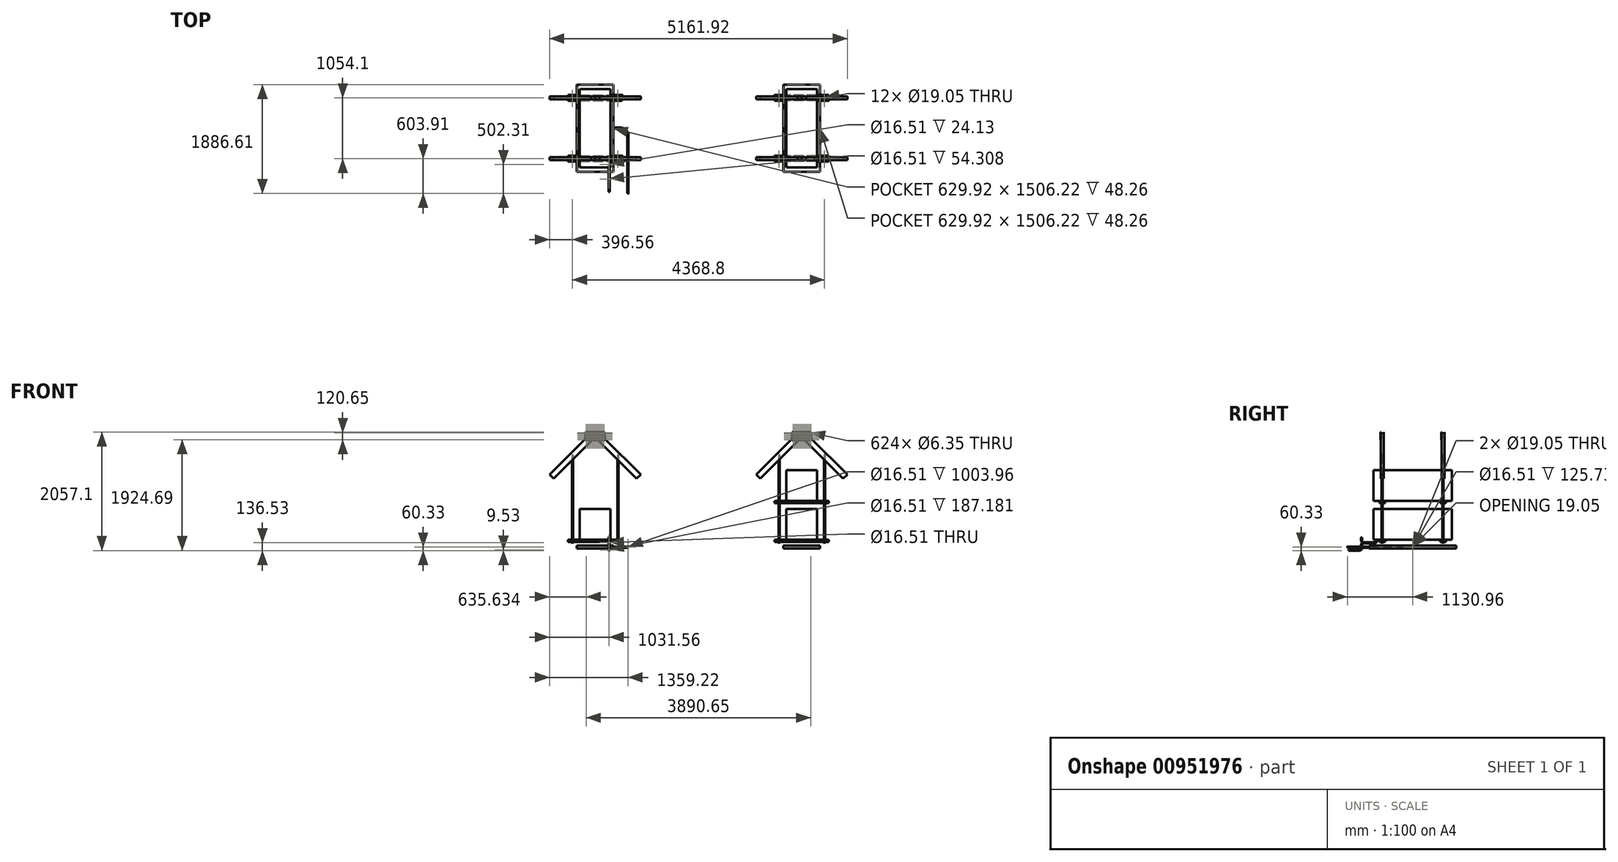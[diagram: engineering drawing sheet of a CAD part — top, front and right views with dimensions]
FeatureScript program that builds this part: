
annotation { "Feature Type Name" : "Feature", "Feature Type Description" : "" }
export const myFeature = defineFeature(function(context is Context, id is Id, definition is map)
    precondition{}
    {
        {
            var Q0;
            Q0=qCreatedBy(makeId("Front.planeOp"),FACE);
            var sketch = newSketch(context, id + "F0", { "sketchPlane" : qUnion([Q0])});
            skLineSegment(sketch, "E0.bottom", {"start": v(-266.7, 266.7) * mm, "end": v(266.7, 266.7) * mm});
            skLineSegment(sketch, "E0.top", {"start": v(-266.7, -266.7) * mm, "end": v(266.7, -266.7) * mm});
            skLineSegment(sketch, "E0.left", {"start": v(-266.7, 266.7) * mm, "end": v(-266.7, -266.7) * mm});
            skLineSegment(sketch, "E0.right", {"start": v(266.7, 266.7) * mm, "end": v(266.7, -266.7) * mm});
            skSolve(sketch);
        }
        {
            var Q0;
            Q0=qSketchRegion(id+"F0",true);
            extrude(context, id + "F1", {"entities" : qUnion([Q0]), "endBound" : BoundingType.SYMMETRIC, "depth" : 1358.9 * mm, "offsetDistance" : 25.4 * mm});
        }
        {
            var Q0;
            Q0=makeQuery(id+"F1.opExtrude","SWEPT_FACE",FACE,{"disambiguationData":[OSD([sQuery(id+"F0.wireOp",EDGE,"E0.top")])]});
            var sketch = newSketch(context, id + "F2", { "sketchPlane" : qUnion([Q0])});
            skLineSegment(sketch, "E1.bottom", {"start": v(-469.9, 577.85) * mm, "end": v(469.9, 577.85) * mm});
            skLineSegment(sketch, "E1.top", {"start": v(-469.9, 476.25) * mm, "end": v(469.9, 476.25) * mm});
            skLineSegment(sketch, "E1.left", {"start": v(-469.9, 577.85) * mm, "end": v(-469.9, 476.25) * mm});
            skLineSegment(sketch, "E1.right", {"start": v(469.9, 577.85) * mm, "end": v(469.9, 476.25) * mm});
            skLineSegment(sketch, "E2.bottom", {"start": v(-469.9, -476.25) * mm, "end": v(469.9, -476.25) * mm});
            skLineSegment(sketch, "E2.top", {"start": v(-469.9, -577.85) * mm, "end": v(469.9, -577.85) * mm});
            skLineSegment(sketch, "E2.left", {"start": v(-469.9, -476.25) * mm, "end": v(-469.9, -577.85) * mm});
            skLineSegment(sketch, "E2.right", {"start": v(469.9, -476.25) * mm, "end": v(469.9, -577.85) * mm});
            skSolve(sketch);
        }
        {
            var Q0;
            Q0=qSketchRegion(id+"F2",true);
            extrude(context, id + "F3", {"entities" : qUnion([Q0]), "operationType" : NewBodyOperationType.ADD, "depth" : 38.1 * mm, "offsetDistance" : 25.4 * mm});
        }
        {
            var Q0;
            {var subQ0=sQuery(id+"F2.wireOp",EDGE,"E1.top");var subQ1=sQuery(id+"F2.wireOp",EDGE,"E1.bottom");var subQ2=sQuery(id+"F2.wireOp",EDGE,"E1.right");Q0=makeQuery(id+"F3.boolean.opBoolean","SPLIT",FACE,{"disambiguationData":[TD([makeQuery(id+"F1.opExtrude","SWEPT_FACE",FACE,{"disambiguationData":[OSD([sQuery(id+"F0.wireOp",EDGE,"E0.right")])]})])],"derivedFrom":makeQuery(id+"F3.opExtrude","CAP_FACE",FACE,{"disambiguationData":[OSD([subQ1,subQ0,sQuery(id+"F2.wireOp",EDGE,"E1.left"),subQ2])],"isStart":true})});}
            var sketch = newSketch(context, id + "F4", { "sketchPlane" : qUnion([Q0])});
            skPoint(sketch, "E3", {"position": v(393.7, -527.05) * mm});
            skPoint(sketch, "E4", {"position": v(-393.7, -527.05) * mm});
            skSolve(sketch);
        }
        {
            var Q0;
            {var subQ0=sQuery(id+"F2.wireOp",EDGE,"E2.top");var subQ1=sQuery(id+"F2.wireOp",EDGE,"E2.bottom");var subQ2=sQuery(id+"F2.wireOp",EDGE,"E2.right");Q0=makeQuery(id+"F3.boolean.opBoolean","SPLIT",FACE,{"disambiguationData":[TD([makeQuery(id+"F1.opExtrude","SWEPT_FACE",FACE,{"disambiguationData":[OSD([sQuery(id+"F0.wireOp",EDGE,"E0.right")])]})])],"derivedFrom":makeQuery(id+"F3.opExtrude","CAP_FACE",FACE,{"disambiguationData":[OSD([subQ1,subQ0,sQuery(id+"F2.wireOp",EDGE,"E2.left"),subQ2])],"isStart":true})});}
            var sketch = newSketch(context, id + "F5", { "sketchPlane" : qUnion([Q0])});
            skPoint(sketch, "E5", {"position": v(393.7, 527.05) * mm});
            skPoint(sketch, "E6", {"position": v(-393.7, 527.05) * mm});
            skSolve(sketch);
        }
        {
            var Q0;
            Q0=sQuery(id+"F4.wireOp",VERTEX,"E3");
            var Q1;
            Q1=sQuery(id+"F4.wireOp",VERTEX,"E4");
            var Q2;
            Q2=sQuery(id+"F5.wireOp",VERTEX,"E5");
            var Q3;
            Q3=sQuery(id+"F5.wireOp",VERTEX,"E6");
            var Q4;
            Q4=makeQuery(id+"F1.opExtrude","SWEPT_BODY",BODY,{"disambiguationData":[OSD([sQuery(id+"F0.wireOp",EDGE,"E0.bottom"),sQuery(id+"F0.wireOp",EDGE,"E0.top"),sQuery(id+"F0.wireOp",EDGE,"E0.left"),sQuery(id+"F0.wireOp",EDGE,"E0.right")])]});
            hole(context, id + "F6", {"style" : HoleStyle.SIMPLE, "endStyle" : HoleEndStyle.THROUGH, "standardTappedOrClearance" : lookupTablePath({ "standard" : "ANSI", "size" : "3/4 (0.75)", "type" : "Drilled" }), "standardBlindInLast" : lookupTablePath({ "standard" : "ANSI", "size" : "3/4 (0.75)", "type" : "Drilled" }), "holeDiameter" : 3 / 101.6 * mm, "majorDiameter" : 6.35 * mm, "isTappedThrough" : true, "tappedDepth" : 12.7 * mm, "tapClearance" : 3, "locations" : qUnion([Q0, Q1, Q2, Q3]), "scope" : qUnion([Q4])});
        }
        {
            var Q0;
            Q0=makeQuery(id+"F3.opExtrude","CAP_EDGE",EDGE,{"disambiguationData":[OSD([sQuery(id+"F2.wireOp",EDGE,"E1.right")])],"isStart":true});
            var Q1;
            Q1=makeQuery(id+"F3.opExtrude","CAP_EDGE",EDGE,{"disambiguationData":[OSD([sQuery(id+"F2.wireOp",EDGE,"E2.right")])],"isStart":true});
            var Q2;
            Q2=makeQuery(id+"F3.opExtrude","CAP_EDGE",EDGE,{"disambiguationData":[OSD([sQuery(id+"F2.wireOp",EDGE,"E1.left")])],"isStart":true});
            var Q3;
            Q3=makeQuery(id+"F3.opExtrude","CAP_EDGE",EDGE,{"disambiguationData":[OSD([sQuery(id+"F2.wireOp",EDGE,"E2.left")])],"isStart":true});
            fillet(context, id + "F7", {"entities" : qUnion([Q0, Q1, Q2, Q3]), "radius" : 12.7 * mm, "tangentPropagation" : true, "allowEdgeOverflow" : false});
        }
        {
            var Q0;
            Q0=makeQuery(id+"F3.opExtrude","CAP_FACE",FACE,{"disambiguationData":[OSD([sQuery(id+"F2.wireOp",EDGE,"E1.bottom"),sQuery(id+"F2.wireOp",EDGE,"E1.top"),sQuery(id+"F2.wireOp",EDGE,"E1.left"),sQuery(id+"F2.wireOp",EDGE,"E1.right")])],"isStart":false});
            cPlane(context, id + "F8", {"entities" : qUnion([Q0]), "cplaneType" : CPlaneType.OFFSET, "offset" : 12.7 * mm, "width" : 152.4 * mm, "height" : 152.4 * mm});
        }
        {
            var Q0;
            Q0=qCreatedBy(id+"F8.planeOp",FACE);
            var sketch = newSketch(context, id + "F9", { "sketchPlane" : qUnion([Q0])});
            skCircle(sketch, "E7.0", {"center": v(393.7, 527.05) * mm, "radius": 9.53 * mm});
            skCircle(sketch, "E8.0", {"center": v(-393.7, 527.05) * mm, "radius": 9.53 * mm});
            skSolve(sketch);
        }
        {
            var Q0;
            Q0=qSketchRegion(id+"F9",true);
            extrude(context, id + "F10", {"entities" : qUnion([Q0]), "operationType" : NewBodyOperationType.ADD, "oppositeDirection" : true, "depth" : 1524 * mm, "offsetDistance" : 25.4 * mm});
        }
        {
            var Q0;
            Q0=makeQuery(id+"F3.opExtrude","CAP_FACE",FACE,{"disambiguationData":[OSD([sQuery(id+"F2.wireOp",EDGE,"E2.bottom"),sQuery(id+"F2.wireOp",EDGE,"E2.top"),sQuery(id+"F2.wireOp",EDGE,"E2.left"),sQuery(id+"F2.wireOp",EDGE,"E2.right")])],"isStart":false});
            cPlane(context, id + "F11", {"entities" : qUnion([Q0]), "cplaneType" : CPlaneType.OFFSET, "offset" : 12.7 * mm, "width" : 152.4 * mm, "height" : 152.4 * mm});
        }
        {
            var Q0;
            Q0=qCreatedBy(id+"F11.planeOp",FACE);
            var sketch = newSketch(context, id + "F12", { "sketchPlane" : qUnion([Q0])});
            skCircle(sketch, "E9.0", {"center": v(-393.7, -527.05) * mm, "radius": 9.53 * mm});
            skCircle(sketch, "E10.0", {"center": v(393.7, -527.05) * mm, "radius": 9.53 * mm});
            skSolve(sketch);
        }
        {
            var Q0;
            Q0=qSketchRegion(id+"F12",true);
            extrude(context, id + "F13", {"entities" : qUnion([Q0]), "oppositeDirection" : true, "depth" : 1524 * mm, "offsetDistance" : 25.4 * mm});
        }
        {
            var Q0;
            Q0=makeQuery(id+"F1.opExtrude","CAP_FACE",FACE,{"disambiguationData":[OSD([sQuery(id+"F0.wireOp",EDGE,"E0.bottom"),sQuery(id+"F0.wireOp",EDGE,"E0.top"),sQuery(id+"F0.wireOp",EDGE,"E0.left"),sQuery(id+"F0.wireOp",EDGE,"E0.right")])],"isStart":false});
            cPlane(context, id + "F14", {"entities" : qUnion([Q0]), "cplaneType" : CPlaneType.OFFSET, "offset" : 152.4 * mm, "oppositeDirection" : true, "width" : 152.4 * mm, "height" : 152.4 * mm});
        }
        {
            var Q0;
            Q0=qCreatedBy(id+"F14.planeOp",FACE);
            var sketch = newSketch(context, id + "F15", { "sketchPlane" : qUnion([Q0])});
            skLineSegment(sketch, "E11", {"start": v(0, 2010.8) * mm, "end": v(0, -441.63) * mm, "construction": true});
            skLineSegment(sketch, "E12", {"start": v(0, 1511.3) * mm, "end": v(718.42, 792.88) * mm});
            skLineSegment(sketch, "E13", {"start": v(718.42, 792.88) * mm, "end": v(790.26, 864.72) * mm});
            skLineSegment(sketch, "E14", {"start": v(0, 1511.3) * mm, "end": v(71.84, 1583.14) * mm});
            skLineSegment(sketch, "E15", {"start": v(790.26, 864.72) * mm, "end": v(71.84, 1583.14) * mm});
            skLineSegment(sketch, "E16", {"start": v(0, 1511.3) * mm, "end": v(-718.42, 792.88) * mm});
            skLineSegment(sketch, "E17", {"start": v(-718.42, 792.88) * mm, "end": v(-790.26, 864.72) * mm});
            skLineSegment(sketch, "E18", {"start": v(0, 1511.3) * mm, "end": v(-71.84, 1583.14) * mm});
            skLineSegment(sketch, "E19", {"start": v(-790.26, 864.72) * mm, "end": v(-71.84, 1583.14) * mm});
            skSolve(sketch);
        }
        {
            var Q0;
            Q0=qSketchRegion(id+"F15",true);
            extrude(context, id + "F16", {"entities" : qUnion([Q0]), "endBound" : BoundingType.SYMMETRIC, "depth" : 50.8 * mm, "offsetDistance" : 25.4 * mm});
        }
        {
            var Q0;
            Q0=makeQuery(id+"F1.opExtrude","CAP_FACE",FACE,{"disambiguationData":[OSD([sQuery(id+"F0.wireOp",EDGE,"E0.bottom"),sQuery(id+"F0.wireOp",EDGE,"E0.top"),sQuery(id+"F0.wireOp",EDGE,"E0.left"),sQuery(id+"F0.wireOp",EDGE,"E0.right")])],"isStart":false});
            cPlane(context, id + "F17", {"entities" : qUnion([Q0]), "cplaneType" : CPlaneType.OFFSET, "offset" : 679.45 * mm, "oppositeDirection" : true, "width" : 152.4 * mm, "height" : 152.4 * mm});
        }
        {
            var Q0;
            Q0=makeQuery(id+"F16.opExtrude","SWEPT_BODY",BODY,{"disambiguationData":[OSD([sQuery(id+"F15.wireOp",EDGE,"E12"),sQuery(id+"F15.wireOp",EDGE,"E13"),sQuery(id+"F15.wireOp",EDGE,"E14"),sQuery(id+"F15.wireOp",EDGE,"E15")])]});
            var Q1;
            Q1=makeQuery(id+"F16.opExtrude","SWEPT_BODY",BODY,{"disambiguationData":[OSD([sQuery(id+"F15.wireOp",EDGE,"E16"),sQuery(id+"F15.wireOp",EDGE,"E17"),sQuery(id+"F15.wireOp",EDGE,"E18"),sQuery(id+"F15.wireOp",EDGE,"E19")])]});
            var Q2;
            Q2=qCreatedBy(id+"F17.planeOp",FACE);
            mirror(context, id + "F18", {"entities" : qUnion([Q0, Q1]), "mirrorPlane" : qUnion([Q2])});
        }
        {
            var Q0;
            Q0=makeQuery(id+"F16.opExtrude","CAP_FACE",FACE,{"disambiguationData":[OSD([sQuery(id+"F15.wireOp",EDGE,"E12"),sQuery(id+"F15.wireOp",EDGE,"E13"),sQuery(id+"F15.wireOp",EDGE,"E14"),sQuery(id+"F15.wireOp",EDGE,"E15")])],"isStart":false});
            var sketch = newSketch(context, id + "F19", { "sketchPlane" : qUnion([Q0])});
            skLineSegment(sketch, "E20.bottom", {"start": v(-165.1, 1603.07) * mm, "end": v(165.1, 1603.07) * mm});
            skLineSegment(sketch, "E20.top", {"start": v(-165.1, 1460.5) * mm, "end": v(165.1, 1460.5) * mm});
            skLineSegment(sketch, "E20.left", {"start": v(-165.1, 1603.07) * mm, "end": v(-165.1, 1460.5) * mm});
            skLineSegment(sketch, "E20.right", {"start": v(165.1, 1603.07) * mm, "end": v(165.1, 1460.5) * mm});
            skCircle(sketch, "E21", {"center": v(-154.63, 1470.66) * mm, "radius": 3.18 * mm});
            skCircle(sketch, "E22.0.1.0", {"center": v(-154.63, 1494.8) * mm, "radius": 3.18 * mm});
            skCircle(sketch, "E22.0.2.0", {"center": v(-154.63, 1518.92) * mm, "radius": 3.18 * mm});
            skCircle(sketch, "E22.0.3.0", {"center": v(-154.63, 1543.05) * mm, "radius": 3.18 * mm});
            skCircle(sketch, "E22.0.4.0", {"center": v(-154.63, 1567.18) * mm, "radius": 3.18 * mm});
            skCircle(sketch, "E22.0.5.0", {"center": v(-154.63, 1591.3) * mm, "radius": 3.18 * mm});
            skCircle(sketch, "E22.1.0.0", {"center": v(-129.23, 1470.66) * mm, "radius": 3.18 * mm});
            skCircle(sketch, "E22.1.1.0", {"center": v(-129.23, 1494.8) * mm, "radius": 3.18 * mm});
            skCircle(sketch, "E22.1.2.0", {"center": v(-129.23, 1518.92) * mm, "radius": 3.18 * mm});
            skCircle(sketch, "E22.1.3.0", {"center": v(-129.23, 1543.05) * mm, "radius": 3.18 * mm});
            skCircle(sketch, "E22.1.4.0", {"center": v(-129.23, 1567.18) * mm, "radius": 3.18 * mm});
            skCircle(sketch, "E22.1.5.0", {"center": v(-129.23, 1591.3) * mm, "radius": 3.18 * mm});
            skCircle(sketch, "E22.2.0.0", {"center": v(-103.83, 1470.66) * mm, "radius": 3.18 * mm});
            skCircle(sketch, "E22.2.1.0", {"center": v(-103.83, 1494.8) * mm, "radius": 3.18 * mm});
            skCircle(sketch, "E22.2.2.0", {"center": v(-103.83, 1518.92) * mm, "radius": 3.18 * mm});
            skCircle(sketch, "E22.2.3.0", {"center": v(-103.83, 1543.05) * mm, "radius": 3.18 * mm});
            skCircle(sketch, "E22.2.4.0", {"center": v(-103.83, 1567.18) * mm, "radius": 3.18 * mm});
            skCircle(sketch, "E22.2.5.0", {"center": v(-103.83, 1591.3) * mm, "radius": 3.18 * mm});
            skCircle(sketch, "E22.3.0.0", {"center": v(-78.43, 1470.66) * mm, "radius": 3.18 * mm});
            skCircle(sketch, "E22.3.1.0", {"center": v(-78.43, 1494.8) * mm, "radius": 3.18 * mm});
            skCircle(sketch, "E22.3.2.0", {"center": v(-78.43, 1518.92) * mm, "radius": 3.18 * mm});
            skCircle(sketch, "E22.3.3.0", {"center": v(-78.43, 1543.05) * mm, "radius": 3.18 * mm});
            skCircle(sketch, "E22.3.4.0", {"center": v(-78.43, 1567.18) * mm, "radius": 3.18 * mm});
            skCircle(sketch, "E22.3.5.0", {"center": v(-78.43, 1591.3) * mm, "radius": 3.18 * mm});
            skCircle(sketch, "E22.4.0.0", {"center": v(-53.03, 1470.66) * mm, "radius": 3.18 * mm});
            skCircle(sketch, "E22.4.1.0", {"center": v(-53.03, 1494.8) * mm, "radius": 3.18 * mm});
            skCircle(sketch, "E22.4.2.0", {"center": v(-53.03, 1518.92) * mm, "radius": 3.18 * mm});
            skCircle(sketch, "E22.4.3.0", {"center": v(-53.03, 1543.05) * mm, "radius": 3.18 * mm});
            skCircle(sketch, "E22.4.4.0", {"center": v(-53.03, 1567.18) * mm, "radius": 3.18 * mm});
            skCircle(sketch, "E22.4.5.0", {"center": v(-53.03, 1591.3) * mm, "radius": 3.18 * mm});
            skCircle(sketch, "E22.5.0.0", {"center": v(-27.63, 1470.66) * mm, "radius": 3.18 * mm});
            skCircle(sketch, "E22.5.1.0", {"center": v(-27.63, 1494.8) * mm, "radius": 3.18 * mm});
            skCircle(sketch, "E22.5.2.0", {"center": v(-27.63, 1518.92) * mm, "radius": 3.18 * mm});
            skCircle(sketch, "E22.5.3.0", {"center": v(-27.63, 1543.05) * mm, "radius": 3.18 * mm});
            skCircle(sketch, "E22.5.4.0", {"center": v(-27.63, 1567.18) * mm, "radius": 3.18 * mm});
            skCircle(sketch, "E22.5.5.0", {"center": v(-27.63, 1591.3) * mm, "radius": 3.18 * mm});
            skCircle(sketch, "E22.6.0.0", {"center": v(-2.23, 1470.66) * mm, "radius": 3.18 * mm});
            skCircle(sketch, "E22.6.1.0", {"center": v(-2.23, 1494.8) * mm, "radius": 3.18 * mm});
            skCircle(sketch, "E22.6.2.0", {"center": v(-2.23, 1518.92) * mm, "radius": 3.18 * mm});
            skCircle(sketch, "E22.6.3.0", {"center": v(-2.23, 1543.05) * mm, "radius": 3.18 * mm});
            skCircle(sketch, "E22.6.4.0", {"center": v(-2.23, 1567.18) * mm, "radius": 3.18 * mm});
            skCircle(sketch, "E22.6.5.0", {"center": v(-2.23, 1591.3) * mm, "radius": 3.18 * mm});
            skCircle(sketch, "E22.7.0.0", {"center": v(23.17, 1470.66) * mm, "radius": 3.18 * mm});
            skCircle(sketch, "E22.7.1.0", {"center": v(23.17, 1494.8) * mm, "radius": 3.18 * mm});
            skCircle(sketch, "E22.7.2.0", {"center": v(23.17, 1518.92) * mm, "radius": 3.18 * mm});
            skCircle(sketch, "E22.7.3.0", {"center": v(23.17, 1543.05) * mm, "radius": 3.18 * mm});
            skCircle(sketch, "E22.7.4.0", {"center": v(23.17, 1567.18) * mm, "radius": 3.18 * mm});
            skCircle(sketch, "E22.7.5.0", {"center": v(23.17, 1591.3) * mm, "radius": 3.18 * mm});
            skCircle(sketch, "E22.8.0.0", {"center": v(48.57, 1470.66) * mm, "radius": 3.18 * mm});
            skCircle(sketch, "E22.8.1.0", {"center": v(48.57, 1494.8) * mm, "radius": 3.18 * mm});
            skCircle(sketch, "E22.8.2.0", {"center": v(48.57, 1518.92) * mm, "radius": 3.18 * mm});
            skCircle(sketch, "E22.8.3.0", {"center": v(48.57, 1543.05) * mm, "radius": 3.18 * mm});
            skCircle(sketch, "E22.8.4.0", {"center": v(48.57, 1567.18) * mm, "radius": 3.18 * mm});
            skCircle(sketch, "E22.8.5.0", {"center": v(48.57, 1591.3) * mm, "radius": 3.18 * mm});
            skCircle(sketch, "E22.9.0.0", {"center": v(73.97, 1470.66) * mm, "radius": 3.18 * mm});
            skCircle(sketch, "E22.9.1.0", {"center": v(73.97, 1494.8) * mm, "radius": 3.18 * mm});
            skCircle(sketch, "E22.9.2.0", {"center": v(73.97, 1518.92) * mm, "radius": 3.18 * mm});
            skCircle(sketch, "E22.9.3.0", {"center": v(73.97, 1543.05) * mm, "radius": 3.18 * mm});
            skCircle(sketch, "E22.9.4.0", {"center": v(73.97, 1567.18) * mm, "radius": 3.18 * mm});
            skCircle(sketch, "E22.9.5.0", {"center": v(73.97, 1591.3) * mm, "radius": 3.18 * mm});
            skCircle(sketch, "E22.10.0.0", {"center": v(99.37, 1470.66) * mm, "radius": 3.18 * mm});
            skCircle(sketch, "E22.10.1.0", {"center": v(99.37, 1494.8) * mm, "radius": 3.18 * mm});
            skCircle(sketch, "E22.10.2.0", {"center": v(99.37, 1518.92) * mm, "radius": 3.18 * mm});
            skCircle(sketch, "E22.10.3.0", {"center": v(99.37, 1543.05) * mm, "radius": 3.18 * mm});
            skCircle(sketch, "E22.10.4.0", {"center": v(99.37, 1567.18) * mm, "radius": 3.18 * mm});
            skCircle(sketch, "E22.10.5.0", {"center": v(99.37, 1591.3) * mm, "radius": 3.18 * mm});
            skCircle(sketch, "E22.11.0.0", {"center": v(124.77, 1470.66) * mm, "radius": 3.18 * mm});
            skCircle(sketch, "E22.11.1.0", {"center": v(124.77, 1494.8) * mm, "radius": 3.18 * mm});
            skCircle(sketch, "E22.11.2.0", {"center": v(124.77, 1518.92) * mm, "radius": 3.18 * mm});
            skCircle(sketch, "E22.11.3.0", {"center": v(124.77, 1543.05) * mm, "radius": 3.18 * mm});
            skCircle(sketch, "E22.11.4.0", {"center": v(124.77, 1567.18) * mm, "radius": 3.18 * mm});
            skCircle(sketch, "E22.11.5.0", {"center": v(124.77, 1591.3) * mm, "radius": 3.18 * mm});
            skCircle(sketch, "E22.12.0.0", {"center": v(150.17, 1470.66) * mm, "radius": 3.18 * mm});
            skCircle(sketch, "E22.12.1.0", {"center": v(150.17, 1494.8) * mm, "radius": 3.18 * mm});
            skCircle(sketch, "E22.12.2.0", {"center": v(150.17, 1518.92) * mm, "radius": 3.18 * mm});
            skCircle(sketch, "E22.12.3.0", {"center": v(150.17, 1543.05) * mm, "radius": 3.18 * mm});
            skCircle(sketch, "E22.12.4.0", {"center": v(150.17, 1567.18) * mm, "radius": 3.18 * mm});
            skCircle(sketch, "E22.12.5.0", {"center": v(150.17, 1591.3) * mm, "radius": 3.18 * mm});
            skLineSegment(sketch, "E22.direction1", {"start": v(-154.63, 1470.66) * mm, "end": v(-129.23, 1470.66) * mm, "construction": true});
            skLineSegment(sketch, "E22.direction2", {"start": v(-154.63, 1470.66) * mm, "end": v(-154.63, 1494.8) * mm, "construction": true});
            skSolve(sketch);
        }
        {
            var Q0;
            Q0=qSketchRegion(id+"F19",true);
            extrude(context, id + "F20", {"entities" : qUnion([Q0]), "depth" : 2.54 * mm, "offsetDistance" : 25.4 * mm});
        }
        {
            var Q0;
            Q0=makeQuery(id+"F16.opExtrude","CAP_FACE",FACE,{"disambiguationData":[OSD([sQuery(id+"F15.wireOp",EDGE,"E12"),sQuery(id+"F15.wireOp",EDGE,"E13"),sQuery(id+"F15.wireOp",EDGE,"E14"),sQuery(id+"F15.wireOp",EDGE,"E15")])],"isStart":true});
            var sketch = newSketch(context, id + "F21", { "sketchPlane" : qUnion([Q0])});
            skLineSegment(sketch, "E23.0.0", {"start": v(165.1, 1460.5) * mm, "end": v(165.1, 1603.07) * mm});
            skLineSegment(sketch, "E23.0.1", {"start": v(165.1, 1603.07) * mm, "end": v(-165.1, 1603.07) * mm});
            skLineSegment(sketch, "E23.0.2", {"start": v(-165.1, 1603.07) * mm, "end": v(-165.1, 1460.5) * mm});
            skLineSegment(sketch, "E23.0.3", {"start": v(-165.1, 1460.5) * mm, "end": v(165.1, 1460.5) * mm});
            skCircle(sketch, "E24.0", {"center": v(154.63, 1591.3) * mm, "radius": 3.18 * mm});
            skCircle(sketch, "E25.0.1.0", {"center": v(154.63, 1567.18) * mm, "radius": 3.18 * mm});
            skCircle(sketch, "E25.0.2.0", {"center": v(154.63, 1543.05) * mm, "radius": 3.18 * mm});
            skCircle(sketch, "E25.0.3.0", {"center": v(154.63, 1518.92) * mm, "radius": 3.18 * mm});
            skCircle(sketch, "E25.0.4.0", {"center": v(154.63, 1494.8) * mm, "radius": 3.18 * mm});
            skCircle(sketch, "E25.0.5.0", {"center": v(154.63, 1470.66) * mm, "radius": 3.18 * mm});
            skCircle(sketch, "E25.1.0.0", {"center": v(129.23, 1591.3) * mm, "radius": 3.18 * mm});
            skCircle(sketch, "E25.1.1.0", {"center": v(129.23, 1567.18) * mm, "radius": 3.18 * mm});
            skCircle(sketch, "E25.1.2.0", {"center": v(129.23, 1543.05) * mm, "radius": 3.18 * mm});
            skCircle(sketch, "E25.1.3.0", {"center": v(129.23, 1518.92) * mm, "radius": 3.18 * mm});
            skCircle(sketch, "E25.1.4.0", {"center": v(129.23, 1494.8) * mm, "radius": 3.18 * mm});
            skCircle(sketch, "E25.1.5.0", {"center": v(129.23, 1470.66) * mm, "radius": 3.18 * mm});
            skCircle(sketch, "E25.2.0.0", {"center": v(103.83, 1591.3) * mm, "radius": 3.18 * mm});
            skCircle(sketch, "E25.2.1.0", {"center": v(103.83, 1567.18) * mm, "radius": 3.18 * mm});
            skCircle(sketch, "E25.2.2.0", {"center": v(103.83, 1543.05) * mm, "radius": 3.18 * mm});
            skCircle(sketch, "E25.2.3.0", {"center": v(103.83, 1518.92) * mm, "radius": 3.18 * mm});
            skCircle(sketch, "E25.2.4.0", {"center": v(103.83, 1494.8) * mm, "radius": 3.18 * mm});
            skCircle(sketch, "E25.2.5.0", {"center": v(103.83, 1470.66) * mm, "radius": 3.18 * mm});
            skCircle(sketch, "E25.3.0.0", {"center": v(78.43, 1591.3) * mm, "radius": 3.18 * mm});
            skCircle(sketch, "E25.3.1.0", {"center": v(78.43, 1567.18) * mm, "radius": 3.18 * mm});
            skCircle(sketch, "E25.3.2.0", {"center": v(78.43, 1543.05) * mm, "radius": 3.18 * mm});
            skCircle(sketch, "E25.3.3.0", {"center": v(78.43, 1518.92) * mm, "radius": 3.18 * mm});
            skCircle(sketch, "E25.3.4.0", {"center": v(78.43, 1494.8) * mm, "radius": 3.18 * mm});
            skCircle(sketch, "E25.3.5.0", {"center": v(78.43, 1470.66) * mm, "radius": 3.18 * mm});
            skCircle(sketch, "E25.4.0.0", {"center": v(53.03, 1591.3) * mm, "radius": 3.18 * mm});
            skCircle(sketch, "E25.4.1.0", {"center": v(53.03, 1567.18) * mm, "radius": 3.18 * mm});
            skCircle(sketch, "E25.4.2.0", {"center": v(53.03, 1543.05) * mm, "radius": 3.18 * mm});
            skCircle(sketch, "E25.4.3.0", {"center": v(53.03, 1518.92) * mm, "radius": 3.18 * mm});
            skCircle(sketch, "E25.4.4.0", {"center": v(53.03, 1494.8) * mm, "radius": 3.18 * mm});
            skCircle(sketch, "E25.4.5.0", {"center": v(53.03, 1470.66) * mm, "radius": 3.18 * mm});
            skCircle(sketch, "E25.5.0.0", {"center": v(27.63, 1591.3) * mm, "radius": 3.18 * mm});
            skCircle(sketch, "E25.5.1.0", {"center": v(27.63, 1567.18) * mm, "radius": 3.18 * mm});
            skCircle(sketch, "E25.5.2.0", {"center": v(27.63, 1543.05) * mm, "radius": 3.18 * mm});
            skCircle(sketch, "E25.5.3.0", {"center": v(27.63, 1518.92) * mm, "radius": 3.18 * mm});
            skCircle(sketch, "E25.5.4.0", {"center": v(27.63, 1494.8) * mm, "radius": 3.18 * mm});
            skCircle(sketch, "E25.5.5.0", {"center": v(27.63, 1470.66) * mm, "radius": 3.18 * mm});
            skCircle(sketch, "E25.6.0.0", {"center": v(2.23, 1591.3) * mm, "radius": 3.18 * mm});
            skCircle(sketch, "E25.6.1.0", {"center": v(2.23, 1567.18) * mm, "radius": 3.18 * mm});
            skCircle(sketch, "E25.6.2.0", {"center": v(2.23, 1543.05) * mm, "radius": 3.18 * mm});
            skCircle(sketch, "E25.6.3.0", {"center": v(2.23, 1518.92) * mm, "radius": 3.18 * mm});
            skCircle(sketch, "E25.6.4.0", {"center": v(2.23, 1494.8) * mm, "radius": 3.18 * mm});
            skCircle(sketch, "E25.6.5.0", {"center": v(2.23, 1470.66) * mm, "radius": 3.18 * mm});
            skCircle(sketch, "E25.7.0.0", {"center": v(-23.17, 1591.3) * mm, "radius": 3.18 * mm});
            skCircle(sketch, "E25.7.1.0", {"center": v(-23.17, 1567.18) * mm, "radius": 3.18 * mm});
            skCircle(sketch, "E25.7.2.0", {"center": v(-23.17, 1543.05) * mm, "radius": 3.18 * mm});
            skCircle(sketch, "E25.7.3.0", {"center": v(-23.17, 1518.92) * mm, "radius": 3.18 * mm});
            skCircle(sketch, "E25.7.4.0", {"center": v(-23.17, 1494.8) * mm, "radius": 3.18 * mm});
            skCircle(sketch, "E25.7.5.0", {"center": v(-23.17, 1470.66) * mm, "radius": 3.18 * mm});
            skCircle(sketch, "E25.8.0.0", {"center": v(-48.57, 1591.3) * mm, "radius": 3.18 * mm});
            skCircle(sketch, "E25.8.1.0", {"center": v(-48.57, 1567.18) * mm, "radius": 3.18 * mm});
            skCircle(sketch, "E25.8.2.0", {"center": v(-48.57, 1543.05) * mm, "radius": 3.18 * mm});
            skCircle(sketch, "E25.8.3.0", {"center": v(-48.57, 1518.92) * mm, "radius": 3.18 * mm});
            skCircle(sketch, "E25.8.4.0", {"center": v(-48.57, 1494.8) * mm, "radius": 3.18 * mm});
            skCircle(sketch, "E25.8.5.0", {"center": v(-48.57, 1470.66) * mm, "radius": 3.18 * mm});
            skCircle(sketch, "E25.9.0.0", {"center": v(-73.97, 1591.3) * mm, "radius": 3.18 * mm});
            skCircle(sketch, "E25.9.1.0", {"center": v(-73.97, 1567.18) * mm, "radius": 3.18 * mm});
            skCircle(sketch, "E25.9.2.0", {"center": v(-73.97, 1543.05) * mm, "radius": 3.18 * mm});
            skCircle(sketch, "E25.9.3.0", {"center": v(-73.97, 1518.92) * mm, "radius": 3.18 * mm});
            skCircle(sketch, "E25.9.4.0", {"center": v(-73.97, 1494.8) * mm, "radius": 3.18 * mm});
            skCircle(sketch, "E25.9.5.0", {"center": v(-73.97, 1470.66) * mm, "radius": 3.18 * mm});
            skCircle(sketch, "E25.10.0.0", {"center": v(-99.37, 1591.3) * mm, "radius": 3.18 * mm});
            skCircle(sketch, "E25.10.1.0", {"center": v(-99.37, 1567.18) * mm, "radius": 3.18 * mm});
            skCircle(sketch, "E25.10.2.0", {"center": v(-99.37, 1543.05) * mm, "radius": 3.18 * mm});
            skCircle(sketch, "E25.10.3.0", {"center": v(-99.37, 1518.92) * mm, "radius": 3.18 * mm});
            skCircle(sketch, "E25.10.4.0", {"center": v(-99.37, 1494.8) * mm, "radius": 3.18 * mm});
            skCircle(sketch, "E25.10.5.0", {"center": v(-99.37, 1470.66) * mm, "radius": 3.18 * mm});
            skCircle(sketch, "E25.11.0.0", {"center": v(-124.77, 1591.3) * mm, "radius": 3.18 * mm});
            skCircle(sketch, "E25.11.1.0", {"center": v(-124.77, 1567.18) * mm, "radius": 3.18 * mm});
            skCircle(sketch, "E25.11.2.0", {"center": v(-124.77, 1543.05) * mm, "radius": 3.18 * mm});
            skCircle(sketch, "E25.11.3.0", {"center": v(-124.77, 1518.92) * mm, "radius": 3.18 * mm});
            skCircle(sketch, "E25.11.4.0", {"center": v(-124.77, 1494.8) * mm, "radius": 3.18 * mm});
            skCircle(sketch, "E25.11.5.0", {"center": v(-124.77, 1470.66) * mm, "radius": 3.18 * mm});
            skCircle(sketch, "E25.12.0.0", {"center": v(-150.17, 1591.3) * mm, "radius": 3.18 * mm});
            skCircle(sketch, "E25.12.1.0", {"center": v(-150.17, 1567.18) * mm, "radius": 3.18 * mm});
            skCircle(sketch, "E25.12.2.0", {"center": v(-150.17, 1543.05) * mm, "radius": 3.18 * mm});
            skCircle(sketch, "E25.12.3.0", {"center": v(-150.17, 1518.92) * mm, "radius": 3.18 * mm});
            skCircle(sketch, "E25.12.4.0", {"center": v(-150.17, 1494.8) * mm, "radius": 3.18 * mm});
            skCircle(sketch, "E25.12.5.0", {"center": v(-150.17, 1470.66) * mm, "radius": 3.18 * mm});
            skLineSegment(sketch, "E25.direction1", {"start": v(154.63, 1591.3) * mm, "end": v(129.23, 1591.3) * mm, "construction": true});
            skLineSegment(sketch, "E25.direction2", {"start": v(154.63, 1591.3) * mm, "end": v(154.63, 1567.18) * mm, "construction": true});
            skSolve(sketch);
        }
        {
            var Q0;
            Q0=qSketchRegion(id+"F21",true);
            extrude(context, id + "F22", {"entities" : qUnion([Q0]), "depth" : 2.54 * mm, "offsetDistance" : 25.4 * mm});
        }
        {
            var Q0;
            Q0=makeQuery(id+"F20.opExtrude","SWEPT_BODY",BODY,{"disambiguationData":[OSD([sQuery(id+"F19.wireOp",EDGE,"E20.bottom"),sQuery(id+"F19.wireOp",EDGE,"E20.top"),sQuery(id+"F19.wireOp",EDGE,"E20.left"),sQuery(id+"F19.wireOp",EDGE,"E20.right"),sQuery(id+"F19.wireOp",EDGE,"E21"),sQuery(id+"F19.wireOp",EDGE,"E22.0.1.0"),sQuery(id+"F19.wireOp",EDGE,"E22.0.2.0"),sQuery(id+"F19.wireOp",EDGE,"E22.0.3.0"),sQuery(id+"F19.wireOp",EDGE,"E22.0.4.0"),sQuery(id+"F19.wireOp",EDGE,"E22.0.5.0"),sQuery(id+"F19.wireOp",EDGE,"E22.1.0.0"),sQuery(id+"F19.wireOp",EDGE,"E22.1.1.0"),sQuery(id+"F19.wireOp",EDGE,"E22.1.2.0"),sQuery(id+"F19.wireOp",EDGE,"E22.1.3.0"),sQuery(id+"F19.wireOp",EDGE,"E22.1.4.0"),sQuery(id+"F19.wireOp",EDGE,"E22.1.5.0"),sQuery(id+"F19.wireOp",EDGE,"E22.2.0.0"),sQuery(id+"F19.wireOp",EDGE,"E22.2.1.0"),sQuery(id+"F19.wireOp",EDGE,"E22.2.2.0"),sQuery(id+"F19.wireOp",EDGE,"E22.2.3.0"),sQuery(id+"F19.wireOp",EDGE,"E22.2.4.0"),sQuery(id+"F19.wireOp",EDGE,"E22.2.5.0"),sQuery(id+"F19.wireOp",EDGE,"E22.3.0.0"),sQuery(id+"F19.wireOp",EDGE,"E22.3.1.0"),sQuery(id+"F19.wireOp",EDGE,"E22.3.2.0"),sQuery(id+"F19.wireOp",EDGE,"E22.3.3.0"),sQuery(id+"F19.wireOp",EDGE,"E22.3.4.0"),sQuery(id+"F19.wireOp",EDGE,"E22.3.5.0"),sQuery(id+"F19.wireOp",EDGE,"E22.4.0.0"),sQuery(id+"F19.wireOp",EDGE,"E22.4.1.0"),sQuery(id+"F19.wireOp",EDGE,"E22.4.2.0"),sQuery(id+"F19.wireOp",EDGE,"E22.4.3.0"),sQuery(id+"F19.wireOp",EDGE,"E22.4.4.0"),sQuery(id+"F19.wireOp",EDGE,"E22.4.5.0"),sQuery(id+"F19.wireOp",EDGE,"E22.5.0.0"),sQuery(id+"F19.wireOp",EDGE,"E22.5.1.0"),sQuery(id+"F19.wireOp",EDGE,"E22.5.2.0"),sQuery(id+"F19.wireOp",EDGE,"E22.5.3.0"),sQuery(id+"F19.wireOp",EDGE,"E22.5.4.0"),sQuery(id+"F19.wireOp",EDGE,"E22.5.5.0"),sQuery(id+"F19.wireOp",EDGE,"E22.6.0.0"),sQuery(id+"F19.wireOp",EDGE,"E22.6.1.0"),sQuery(id+"F19.wireOp",EDGE,"E22.6.2.0"),sQuery(id+"F19.wireOp",EDGE,"E22.6.3.0"),sQuery(id+"F19.wireOp",EDGE,"E22.6.4.0"),sQuery(id+"F19.wireOp",EDGE,"E22.6.5.0"),sQuery(id+"F19.wireOp",EDGE,"E22.7.0.0"),sQuery(id+"F19.wireOp",EDGE,"E22.7.1.0"),sQuery(id+"F19.wireOp",EDGE,"E22.7.2.0"),sQuery(id+"F19.wireOp",EDGE,"E22.7.3.0"),sQuery(id+"F19.wireOp",EDGE,"E22.7.4.0"),sQuery(id+"F19.wireOp",EDGE,"E22.7.5.0"),sQuery(id+"F19.wireOp",EDGE,"E22.8.0.0"),sQuery(id+"F19.wireOp",EDGE,"E22.8.1.0"),sQuery(id+"F19.wireOp",EDGE,"E22.8.2.0"),sQuery(id+"F19.wireOp",EDGE,"E22.8.3.0"),sQuery(id+"F19.wireOp",EDGE,"E22.8.4.0"),sQuery(id+"F19.wireOp",EDGE,"E22.8.5.0"),sQuery(id+"F19.wireOp",EDGE,"E22.9.0.0"),sQuery(id+"F19.wireOp",EDGE,"E22.9.1.0"),sQuery(id+"F19.wireOp",EDGE,"E22.9.2.0"),sQuery(id+"F19.wireOp",EDGE,"E22.9.3.0"),sQuery(id+"F19.wireOp",EDGE,"E22.9.4.0"),sQuery(id+"F19.wireOp",EDGE,"E22.9.5.0"),sQuery(id+"F19.wireOp",EDGE,"E22.10.0.0"),sQuery(id+"F19.wireOp",EDGE,"E22.10.1.0"),sQuery(id+"F19.wireOp",EDGE,"E22.10.2.0"),sQuery(id+"F19.wireOp",EDGE,"E22.10.3.0"),sQuery(id+"F19.wireOp",EDGE,"E22.10.4.0"),sQuery(id+"F19.wireOp",EDGE,"E22.10.5.0"),sQuery(id+"F19.wireOp",EDGE,"E22.11.0.0"),sQuery(id+"F19.wireOp",EDGE,"E22.11.1.0"),sQuery(id+"F19.wireOp",EDGE,"E22.11.2.0"),sQuery(id+"F19.wireOp",EDGE,"E22.11.3.0"),sQuery(id+"F19.wireOp",EDGE,"E22.11.4.0"),sQuery(id+"F19.wireOp",EDGE,"E22.11.5.0"),sQuery(id+"F19.wireOp",EDGE,"E22.12.0.0"),sQuery(id+"F19.wireOp",EDGE,"E22.12.1.0"),sQuery(id+"F19.wireOp",EDGE,"E22.12.2.0"),sQuery(id+"F19.wireOp",EDGE,"E22.12.3.0"),sQuery(id+"F19.wireOp",EDGE,"E22.12.4.0"),sQuery(id+"F19.wireOp",EDGE,"E22.12.5.0")])]});
            var Q1;
            Q1=makeQuery(id+"F22.opExtrude","SWEPT_BODY",BODY,{"disambiguationData":[OSD([sQuery(id+"F21.wireOp",EDGE,"E23.0.0"),sQuery(id+"F21.wireOp",EDGE,"E23.0.1"),sQuery(id+"F21.wireOp",EDGE,"E23.0.2"),sQuery(id+"F21.wireOp",EDGE,"E23.0.3"),sQuery(id+"F21.wireOp",EDGE,"E24.0"),sQuery(id+"F21.wireOp",EDGE,"E25.0.1.0"),sQuery(id+"F21.wireOp",EDGE,"E25.0.2.0"),sQuery(id+"F21.wireOp",EDGE,"E25.0.3.0"),sQuery(id+"F21.wireOp",EDGE,"E25.0.4.0"),sQuery(id+"F21.wireOp",EDGE,"E25.0.5.0"),sQuery(id+"F21.wireOp",EDGE,"E25.1.0.0"),sQuery(id+"F21.wireOp",EDGE,"E25.1.1.0"),sQuery(id+"F21.wireOp",EDGE,"E25.1.2.0"),sQuery(id+"F21.wireOp",EDGE,"E25.1.3.0"),sQuery(id+"F21.wireOp",EDGE,"E25.1.4.0"),sQuery(id+"F21.wireOp",EDGE,"E25.1.5.0"),sQuery(id+"F21.wireOp",EDGE,"E25.2.0.0"),sQuery(id+"F21.wireOp",EDGE,"E25.2.1.0"),sQuery(id+"F21.wireOp",EDGE,"E25.2.2.0"),sQuery(id+"F21.wireOp",EDGE,"E25.2.3.0"),sQuery(id+"F21.wireOp",EDGE,"E25.2.4.0"),sQuery(id+"F21.wireOp",EDGE,"E25.2.5.0"),sQuery(id+"F21.wireOp",EDGE,"E25.3.0.0"),sQuery(id+"F21.wireOp",EDGE,"E25.3.1.0"),sQuery(id+"F21.wireOp",EDGE,"E25.3.2.0"),sQuery(id+"F21.wireOp",EDGE,"E25.3.3.0"),sQuery(id+"F21.wireOp",EDGE,"E25.3.4.0"),sQuery(id+"F21.wireOp",EDGE,"E25.3.5.0"),sQuery(id+"F21.wireOp",EDGE,"E25.4.0.0"),sQuery(id+"F21.wireOp",EDGE,"E25.4.1.0"),sQuery(id+"F21.wireOp",EDGE,"E25.4.2.0"),sQuery(id+"F21.wireOp",EDGE,"E25.4.3.0"),sQuery(id+"F21.wireOp",EDGE,"E25.4.4.0"),sQuery(id+"F21.wireOp",EDGE,"E25.4.5.0"),sQuery(id+"F21.wireOp",EDGE,"E25.5.0.0"),sQuery(id+"F21.wireOp",EDGE,"E25.5.1.0"),sQuery(id+"F21.wireOp",EDGE,"E25.5.2.0"),sQuery(id+"F21.wireOp",EDGE,"E25.5.3.0"),sQuery(id+"F21.wireOp",EDGE,"E25.5.4.0"),sQuery(id+"F21.wireOp",EDGE,"E25.5.5.0"),sQuery(id+"F21.wireOp",EDGE,"E25.6.0.0"),sQuery(id+"F21.wireOp",EDGE,"E25.6.1.0"),sQuery(id+"F21.wireOp",EDGE,"E25.6.2.0"),sQuery(id+"F21.wireOp",EDGE,"E25.6.3.0"),sQuery(id+"F21.wireOp",EDGE,"E25.6.4.0"),sQuery(id+"F21.wireOp",EDGE,"E25.6.5.0"),sQuery(id+"F21.wireOp",EDGE,"E25.7.0.0"),sQuery(id+"F21.wireOp",EDGE,"E25.7.1.0"),sQuery(id+"F21.wireOp",EDGE,"E25.7.2.0"),sQuery(id+"F21.wireOp",EDGE,"E25.7.3.0"),sQuery(id+"F21.wireOp",EDGE,"E25.7.4.0"),sQuery(id+"F21.wireOp",EDGE,"E25.7.5.0"),sQuery(id+"F21.wireOp",EDGE,"E25.8.0.0"),sQuery(id+"F21.wireOp",EDGE,"E25.8.1.0"),sQuery(id+"F21.wireOp",EDGE,"E25.8.2.0"),sQuery(id+"F21.wireOp",EDGE,"E25.8.3.0"),sQuery(id+"F21.wireOp",EDGE,"E25.8.4.0"),sQuery(id+"F21.wireOp",EDGE,"E25.8.5.0"),sQuery(id+"F21.wireOp",EDGE,"E25.9.0.0"),sQuery(id+"F21.wireOp",EDGE,"E25.9.1.0"),sQuery(id+"F21.wireOp",EDGE,"E25.9.2.0"),sQuery(id+"F21.wireOp",EDGE,"E25.9.3.0"),sQuery(id+"F21.wireOp",EDGE,"E25.9.4.0"),sQuery(id+"F21.wireOp",EDGE,"E25.9.5.0"),sQuery(id+"F21.wireOp",EDGE,"E25.10.0.0"),sQuery(id+"F21.wireOp",EDGE,"E25.10.1.0"),sQuery(id+"F21.wireOp",EDGE,"E25.10.2.0"),sQuery(id+"F21.wireOp",EDGE,"E25.10.3.0"),sQuery(id+"F21.wireOp",EDGE,"E25.10.4.0"),sQuery(id+"F21.wireOp",EDGE,"E25.10.5.0"),sQuery(id+"F21.wireOp",EDGE,"E25.11.0.0"),sQuery(id+"F21.wireOp",EDGE,"E25.11.1.0"),sQuery(id+"F21.wireOp",EDGE,"E25.11.2.0"),sQuery(id+"F21.wireOp",EDGE,"E25.11.3.0"),sQuery(id+"F21.wireOp",EDGE,"E25.11.4.0"),sQuery(id+"F21.wireOp",EDGE,"E25.11.5.0"),sQuery(id+"F21.wireOp",EDGE,"E25.12.0.0"),sQuery(id+"F21.wireOp",EDGE,"E25.12.1.0"),sQuery(id+"F21.wireOp",EDGE,"E25.12.2.0"),sQuery(id+"F21.wireOp",EDGE,"E25.12.3.0"),sQuery(id+"F21.wireOp",EDGE,"E25.12.4.0"),sQuery(id+"F21.wireOp",EDGE,"E25.12.5.0")])]});
            var Q2;
            Q2=qCreatedBy(id+"F17.planeOp",FACE);
            mirror(context, id + "F23", {"entities" : qUnion([Q0, Q1]), "mirrorPlane" : qUnion([Q2])});
        }
        {
            var Q0;
            Q0=makeQuery(id+"F10.opExtrude","CAP_FACE",FACE,{"disambiguationData":[OSD([sQuery(id+"F9.wireOp",EDGE,"E7.0")])],"isStart":true});
            var sketch = newSketch(context, id + "F24", { "sketchPlane" : qUnion([Q0])});
            skCircle(sketch, "E26.0", {"center": v(393.7, 527.05) * mm, "radius": 9.53 * mm});
            skCircle(sketch, "E27.cCircle", {"center": v(393.7, 527.05) * mm, "radius": 19.05 * mm, "construction": true});
            skLineSegment(sketch, "E27.0", {"start": v(412.75, 538.05) * mm, "end": v(412.75, 516.05) * mm});
            skLineSegment(sketch, "E27.1", {"start": v(412.75, 516.05) * mm, "end": v(393.7, 505.05) * mm});
            skLineSegment(sketch, "E27.2", {"start": v(393.7, 505.05) * mm, "end": v(374.65, 516.05) * mm});
            skLineSegment(sketch, "E27.3", {"start": v(374.65, 516.05) * mm, "end": v(374.65, 538.05) * mm});
            skLineSegment(sketch, "E27.4", {"start": v(374.65, 538.05) * mm, "end": v(393.7, 549.05) * mm});
            skLineSegment(sketch, "E27.5", {"start": v(393.7, 549.05) * mm, "end": v(412.75, 538.05) * mm});
            skPoint(sketch, "E27.0.midPoint", {"position": v(412.75, 527.05) * mm});
            skCircle(sketch, "E28.0", {"center": v(-393.7, 527.05) * mm, "radius": 9.53 * mm});
            skCircle(sketch, "E29.0", {"center": v(-393.7, -527.05) * mm, "radius": 9.53 * mm});
            skCircle(sketch, "E30.0", {"center": v(393.7, -527.05) * mm, "radius": 9.53 * mm});
            skCircle(sketch, "E31.cCircle", {"center": v(-393.7, 527.05) * mm, "radius": 19.05 * mm, "construction": true});
            skLineSegment(sketch, "E31.0", {"start": v(-374.65, 538.05) * mm, "end": v(-374.65, 516.05) * mm});
            skLineSegment(sketch, "E31.1", {"start": v(-374.65, 516.05) * mm, "end": v(-393.7, 505.05) * mm});
            skLineSegment(sketch, "E31.2", {"start": v(-393.7, 505.05) * mm, "end": v(-412.75, 516.05) * mm});
            skLineSegment(sketch, "E31.3", {"start": v(-412.75, 516.05) * mm, "end": v(-412.75, 538.05) * mm});
            skLineSegment(sketch, "E31.4", {"start": v(-412.75, 538.05) * mm, "end": v(-393.7, 549.05) * mm});
            skLineSegment(sketch, "E31.5", {"start": v(-393.7, 549.05) * mm, "end": v(-374.65, 538.05) * mm});
            skPoint(sketch, "E31.0.midPoint", {"position": v(-374.65, 527.05) * mm});
            skCircle(sketch, "E32.cCircle", {"center": v(-393.7, -527.05) * mm, "radius": 19.05 * mm, "construction": true});
            skLineSegment(sketch, "E32.0", {"start": v(-374.65, -516.05) * mm, "end": v(-374.65, -538.05) * mm});
            skLineSegment(sketch, "E32.1", {"start": v(-374.65, -538.05) * mm, "end": v(-393.7, -549.05) * mm});
            skLineSegment(sketch, "E32.2", {"start": v(-393.7, -549.05) * mm, "end": v(-412.75, -538.05) * mm});
            skLineSegment(sketch, "E32.3", {"start": v(-412.75, -538.05) * mm, "end": v(-412.75, -516.05) * mm});
            skLineSegment(sketch, "E32.4", {"start": v(-412.75, -516.05) * mm, "end": v(-393.7, -505.05) * mm});
            skLineSegment(sketch, "E32.5", {"start": v(-393.7, -505.05) * mm, "end": v(-374.65, -516.05) * mm});
            skPoint(sketch, "E32.0.midPoint", {"position": v(-374.65, -527.05) * mm});
            skCircle(sketch, "E33.cCircle", {"center": v(393.7, -527.05) * mm, "radius": 19.05 * mm, "construction": true});
            skLineSegment(sketch, "E33.0", {"start": v(412.75, -516.05) * mm, "end": v(412.75, -538.05) * mm});
            skLineSegment(sketch, "E33.1", {"start": v(412.75, -538.05) * mm, "end": v(393.7, -549.05) * mm});
            skLineSegment(sketch, "E33.2", {"start": v(393.7, -549.05) * mm, "end": v(374.65, -538.05) * mm});
            skLineSegment(sketch, "E33.3", {"start": v(374.65, -538.05) * mm, "end": v(374.65, -516.05) * mm});
            skLineSegment(sketch, "E33.4", {"start": v(374.65, -516.05) * mm, "end": v(393.7, -505.05) * mm});
            skLineSegment(sketch, "E33.5", {"start": v(393.7, -505.05) * mm, "end": v(412.75, -516.05) * mm});
            skPoint(sketch, "E33.0.midPoint", {"position": v(412.75, -527.05) * mm});
            skSolve(sketch);
        }
        {
            var Q0;
            Q0=qSketchRegion(id+"F24",true);
            extrude(context, id + "F25", {"entities" : qUnion([Q0]), "endBound" : BoundingType.UP_TO_NEXT, "oppositeDirection" : true, "depth" : 25.4 * mm, "offsetDistance" : 25.4 * mm});
        }
        {
            var Q0;
            {var subQ0=sQuery(id+"F2.wireOp",EDGE,"E1.top");Q0=makeQuery(id+"F3.boolean.opBoolean","SPLIT",FACE,{"disambiguationData":[TD([makeQuery(id+"F3.opExtrude","SWEPT_FACE",FACE,{"disambiguationData":[OSD([subQ0])]})])],"derivedFrom":makeQuery(id+"F1.opExtrude","SWEPT_FACE",FACE,{"disambiguationData":[OSD([sQuery(id+"F0.wireOp",EDGE,"E0.top")])]})});}
            cPlane(context, id + "F26", {"entities" : qUnion([Q0]), "cplaneType" : CPlaneType.OFFSET, "offset" : 101.6 * mm, "width" : 152.4 * mm, "height" : 152.4 * mm});
        }
        {
            var Q0;
            Q0=qCreatedBy(id+"F26.planeOp",FACE);
            var sketch = newSketch(context, id + "F27", { "sketchPlane" : qUnion([Q0])});
            skLineSegment(sketch, "E34.bottom", {"start": v(-317.5, 755.65) * mm, "end": v(317.5, 755.65) * mm});
            skLineSegment(sketch, "E34.top", {"start": v(-317.5, -755.65) * mm, "end": v(317.5, -755.65) * mm});
            skLineSegment(sketch, "E34.left", {"start": v(-317.5, 755.65) * mm, "end": v(-317.5, -755.65) * mm});
            skLineSegment(sketch, "E34.right", {"start": v(317.5, 755.65) * mm, "end": v(317.5, -755.65) * mm});
            skSolve(sketch);
        }
        {
            var Q0;
            Q0=qSketchRegion(id+"F27",true);
            extrude(context, id + "F28", {"entities" : qUnion([Q0]), "depth" : 50.8 * mm, "offsetDistance" : 25.4 * mm});
        }
        {
            var Q0;
            Q0=makeQuery(id+"F28.opExtrude","CAP_FACE",FACE,{"disambiguationData":[OSD([sQuery(id+"F27.wireOp",EDGE,"E34.bottom"),sQuery(id+"F27.wireOp",EDGE,"E34.top"),sQuery(id+"F27.wireOp",EDGE,"E34.left"),sQuery(id+"F27.wireOp",EDGE,"E34.right")])],"isStart":true});
            shell(context, id + "F29", {"entities" : qUnion([Q0]), "thickness" : 2.54 * mm});
        }
        {
            var Q0;
            Q0=makeQuery(id+"F29.opShell","OFFSET_FACE",FACE,{"disambiguationData":[OSD([sQuery(id+"F27.wireOp",EDGE,"E34.right")])]});
            var sketch = newSketch(context, id + "F30", { "sketchPlane" : qUnion([Q0])});
            skCircle(sketch, "E35", {"center": v(0, -393.7) * mm, "radius": 9.53 * mm});
            skSolve(sketch);
        }
        {
            var Q0;
            Q0=qSketchRegion(id+"F30",true);
            var Q1;
            Q1=sQuery(id+"F30.wireOp",EDGE,"E35");
            extrude(context, id + "F31", {"entities" : qUnion([Q0]), "operationType" : NewBodyOperationType.REMOVE, "surfaceEntities" : qUnion([Q1]), "endBound" : BoundingType.UP_TO_NEXT, "oppositeDirection" : true, "depth" : 25.4 * mm, "offsetDistance" : 25.4 * mm});
        }
        {
            var Q0;
            Q0=qCreatedBy(id+"F26.planeOp",FACE);
            cPlane(context, id + "F32", {"entities" : qUnion([Q0]), "cplaneType" : CPlaneType.OFFSET, "offset" : 25.4 * mm, "width" : 152.4 * mm, "height" : 152.4 * mm});
        }
        {
            var Q0;
            Q0=qCreatedBy(id+"F32.planeOp",FACE);
            var sketch = newSketch(context, id + "F33", { "sketchPlane" : qUnion([Q0])});
            skLineSegment(sketch, "E36", {"start": v(314.96, 0) * mm, "end": v(441.96, 0) * mm});
            skLineSegment(sketch, "E37", {"start": v(568.96, 127) * mm, "end": v(568.96, 1130.96) * mm});
            skPoint(sketch, "E38.visualSharp", {"position": v(568.96, 0) * mm});
            skArc(sketch, "E38.filletArc", {"start": v(441.96, 0) * mm, "mid": v(531.76, 37.2) * mm, "end": v(568.96, 127) * mm});
            skSolve(sketch);
        }
        {
            var Q0;
            Q0=qSketchRegion(id+"F30",true);
            var Q1;
            Q1=qConstructionFilter(qBodyType(qCreatedBy(id+"F33",EDGE),BodyType.WIRE),ConstructionObject.NO);
            sweep(context, id + "F34", {"profiles" : qUnion([Q0]), "path" : qUnion([Q1])});
        }
        {
            var Q0;
            {var subQ0=sQuery(id+"F2.wireOp",EDGE,"E1.bottom");var subQ3=sQuery(id+"F0.wireOp",EDGE,"E0.top");Q0=makeQuery(id+"F3.boolean.opBoolean","SPLIT",FACE,{"disambiguationData":[TD([makeQuery(id+"F3.opExtrude","SWEPT_FACE",FACE,{"disambiguationData":[OSD([subQ0])]})])],"derivedFrom":makeQuery(id+"F1.opExtrude","SWEPT_FACE",FACE,{"disambiguationData":[OSD([subQ3])]})});}
            var sketch = newSketch(context, id + "F35", { "sketchPlane" : qUnion([Q0])});
            skCircle(sketch, "E39", {"center": v(241.3, 628.65) * mm, "radius": 9.53 * mm});
            skSolve(sketch);
        }
        {
            var Q0;
            Q0=makeQuery(id+"F1.opExtrude","SWEPT_FACE",FACE,{"disambiguationData":[OSD([sQuery(id+"F0.wireOp",EDGE,"E0.right")])]});
            cPlane(context, id + "F36", {"entities" : qUnion([Q0]), "cplaneType" : CPlaneType.OFFSET, "offset" : 25.4 * mm, "oppositeDirection" : true, "width" : 152.4 * mm, "height" : 152.4 * mm});
        }
        {
            var Q0;
            Q0=qCreatedBy(id+"F36.planeOp",FACE);
            var sketch = newSketch(context, id + "F37", { "sketchPlane" : qUnion([Q0])});
            skLineSegment(sketch, "E40", {"start": v(-628.65, -266.7) * mm, "end": v(-628.65, -292.1) * mm});
            skLineSegment(sketch, "E41", {"start": v(-654.05, -317.5) * mm, "end": v(-844.55, -317.5) * mm});
            skLineSegment(sketch, "E42", {"start": v(-882.65, -355.6) * mm, "end": v(-882.65, -406.4) * mm});
            skLineSegment(sketch, "E43", {"start": v(-920.75, -444.5) * mm, "end": v(-1107.93, -444.5) * mm});
            skPoint(sketch, "E44.visualSharp", {"position": v(-628.65, -317.5) * mm});
            skArc(sketch, "E44.filletArc", {"start": v(-654.05, -317.5) * mm, "mid": v(-636.09, -310.06) * mm, "end": v(-628.65, -292.1) * mm});
            skPoint(sketch, "E45.visualSharp", {"position": v(-882.65, -317.5) * mm});
            skLineSegment(sketch, "E46", {"start": v(-844.55, -317.5) * mm, "end": v(-844.55, -317.5) * mm});
            skArc(sketch, "E47.filletArc", {"start": v(-844.55, -317.5) * mm, "mid": v(-871.5, -328.66) * mm, "end": v(-882.65, -355.6) * mm});
            skPoint(sketch, "E48.visualSharp", {"position": v(-882.65, -444.5) * mm});
            skArc(sketch, "E48.filletArc", {"start": v(-920.75, -444.5) * mm, "mid": v(-893.8, -433.34) * mm, "end": v(-882.65, -406.4) * mm});
            skSolve(sketch);
        }
        {
            var Q0;
            Q0=qSketchRegion(id+"F35",true);
            var Q1;
            Q1=qConstructionFilter(qBodyType(qCreatedBy(id+"F37",EDGE),BodyType.WIRE),ConstructionObject.NO);
            sweep(context, id + "F38", {"profiles" : qUnion([Q0]), "path" : qUnion([Q1])});
        }
        {
            var Q0;
            Q0=makeQuery(id+"F34.opSweep","CAP_FACE",FACE,{"disambiguationData":[OSD([sQuery(id+"F30.wireOp",EDGE,"E35"),sQuery(id+"F33.wireOp",VERTEX,"E37.end")])],"isStart":false});
            shell(context, id + "F39", {"entities" : qUnion([Q0]), "thickness" : 1.27 * mm});
        }
        {
            var Q0;
            Q0=qCreatedBy(id+"F36.planeOp",FACE);
            var sketch = newSketch(context, id + "F40", { "sketchPlane" : qUnion([Q0])});
            skLineSegment(sketch, "E49.0", {"start": v(-844.55, -327.03) * mm, "end": v(-844.55, -307.98) * mm, "construction": true});
            skLineSegment(sketch, "E50", {"start": v(-844.55, -317.5) * mm, "end": v(-844.55, -317.5) * mm});
            skLineSegment(sketch, "E51", {"start": v(-882.65, -279.4) * mm, "end": v(-882.65, -225.1) * mm});
            skArc(sketch, "E52.filletArc", {"start": v(-882.65, -279.4) * mm, "mid": v(-871.5, -306.34) * mm, "end": v(-844.55, -317.5) * mm});
            skSolve(sketch);
        }
        {
            var Q0;
            Q0=makeQuery(id+"F1.opExtrude","CAP_FACE",FACE,{"disambiguationData":[OSD([sQuery(id+"F0.wireOp",EDGE,"E0.bottom"),sQuery(id+"F0.wireOp",EDGE,"E0.top"),sQuery(id+"F0.wireOp",EDGE,"E0.left"),sQuery(id+"F0.wireOp",EDGE,"E0.right")])],"isStart":false});
            cPlane(context, id + "F41", {"entities" : qUnion([Q0]), "cplaneType" : CPlaneType.OFFSET, "offset" : 165.1 * mm, "width" : 152.4 * mm, "height" : 152.4 * mm});
        }
        {
            var Q0;
            Q0=qCreatedBy(id+"F41.planeOp",FACE);
            var sketch = newSketch(context, id + "F42", { "sketchPlane" : qUnion([Q0])});
            skCircle(sketch, "E53.0", {"center": v(241.3, -317.5) * mm, "radius": 9.52 * mm});
            skSolve(sketch);
        }
        {
            var Q0;
            Q0=qSketchRegion(id+"F42",true);
            var Q1;
            Q1=qConstructionFilter(qBodyType(qCreatedBy(id+"F40",EDGE),BodyType.WIRE),ConstructionObject.NO);
            sweep(context, id + "F43", {"operationType" : NewBodyOperationType.ADD, "profiles" : qUnion([Q0]), "path" : qUnion([Q1])});
        }
        {
            var Q0;
            Q0=makeQuery(id+"F43.opSweep","CAP_FACE",FACE,{"disambiguationData":[OSD([sQuery(id+"F40.wireOp",VERTEX,"E51.end"),sQuery(id+"F42.wireOp",EDGE,"E53.0")])],"isStart":false});
            var Q1;
            Q1=makeQuery(id+"F38.opSweep","CAP_FACE",FACE,{"disambiguationData":[OSD([sQuery(id+"F35.wireOp",EDGE,"E39"),sQuery(id+"F37.wireOp",VERTEX,"E43.end")])],"isStart":false});
            shell(context, id + "F44", {"entities" : qUnion([Q0, Q1]), "thickness" : 1.27 * mm});
        }
        {
            var Q0;
            Q0=makeQuery(id+"F1.opExtrude","SWEPT_FACE",FACE,{"disambiguationData":[OSD([sQuery(id+"F0.wireOp",EDGE,"E0.right")])]});
            cPlane(context, id + "F45", {"entities" : qUnion([Q0]), "cplaneType" : CPlaneType.OFFSET, "offset" : 1524 * mm, "width" : 152.4 * mm, "height" : 152.4 * mm});
        }
        {
            var Q0;
            Q0=makeQuery(id+"F1.opExtrude","SWEPT_BODY",BODY,{"disambiguationData":[OSD([sQuery(id+"F0.wireOp",EDGE,"E0.bottom"),sQuery(id+"F0.wireOp",EDGE,"E0.top"),sQuery(id+"F0.wireOp",EDGE,"E0.left"),sQuery(id+"F0.wireOp",EDGE,"E0.right")])]});
            var Q1;
            Q1=makeQuery(id+"F13.opExtrude","SWEPT_BODY",BODY,{"disambiguationData":[OSD([sQuery(id+"F12.wireOp",EDGE,"E9.0")])]});
            var Q2;
            Q2=makeQuery(id+"F13.opExtrude","SWEPT_BODY",BODY,{"disambiguationData":[OSD([sQuery(id+"F12.wireOp",EDGE,"E10.0")])]});
            var Q3;
            Q3=makeQuery(id+"F16.opExtrude","SWEPT_BODY",BODY,{"disambiguationData":[OSD([sQuery(id+"F15.wireOp",EDGE,"E12"),sQuery(id+"F15.wireOp",EDGE,"E13"),sQuery(id+"F15.wireOp",EDGE,"E14"),sQuery(id+"F15.wireOp",EDGE,"E15")])]});
            var Q4;
            Q4=makeQuery(id+"F16.opExtrude","SWEPT_BODY",BODY,{"disambiguationData":[OSD([sQuery(id+"F15.wireOp",EDGE,"E16"),sQuery(id+"F15.wireOp",EDGE,"E17"),sQuery(id+"F15.wireOp",EDGE,"E18"),sQuery(id+"F15.wireOp",EDGE,"E19")])]});
            var Q5;
            Q5=makeQuery(id+"F18.opPattern","COPY",BODY,{"derivedFrom":makeQuery(id+"F16.opExtrude","SWEPT_BODY",BODY,{"disambiguationData":[OSD([sQuery(id+"F15.wireOp",EDGE,"E12"),sQuery(id+"F15.wireOp",EDGE,"E13"),sQuery(id+"F15.wireOp",EDGE,"E14"),sQuery(id+"F15.wireOp",EDGE,"E15")])]}),"instanceName":"1"});
            var Q6;
            Q6=makeQuery(id+"F18.opPattern","COPY",BODY,{"derivedFrom":makeQuery(id+"F16.opExtrude","SWEPT_BODY",BODY,{"disambiguationData":[OSD([sQuery(id+"F15.wireOp",EDGE,"E16"),sQuery(id+"F15.wireOp",EDGE,"E17"),sQuery(id+"F15.wireOp",EDGE,"E18"),sQuery(id+"F15.wireOp",EDGE,"E19")])]}),"instanceName":"1"});
            var Q7;
            Q7=makeQuery(id+"F20.opExtrude","SWEPT_BODY",BODY,{"disambiguationData":[OSD([sQuery(id+"F19.wireOp",EDGE,"E20.bottom"),sQuery(id+"F19.wireOp",EDGE,"E20.top"),sQuery(id+"F19.wireOp",EDGE,"E20.left"),sQuery(id+"F19.wireOp",EDGE,"E20.right"),sQuery(id+"F19.wireOp",EDGE,"E21"),sQuery(id+"F19.wireOp",EDGE,"E22.0.1.0"),sQuery(id+"F19.wireOp",EDGE,"E22.0.2.0"),sQuery(id+"F19.wireOp",EDGE,"E22.0.3.0"),sQuery(id+"F19.wireOp",EDGE,"E22.0.4.0"),sQuery(id+"F19.wireOp",EDGE,"E22.0.5.0"),sQuery(id+"F19.wireOp",EDGE,"E22.1.0.0"),sQuery(id+"F19.wireOp",EDGE,"E22.1.1.0"),sQuery(id+"F19.wireOp",EDGE,"E22.1.2.0"),sQuery(id+"F19.wireOp",EDGE,"E22.1.3.0"),sQuery(id+"F19.wireOp",EDGE,"E22.1.4.0"),sQuery(id+"F19.wireOp",EDGE,"E22.1.5.0"),sQuery(id+"F19.wireOp",EDGE,"E22.2.0.0"),sQuery(id+"F19.wireOp",EDGE,"E22.2.1.0"),sQuery(id+"F19.wireOp",EDGE,"E22.2.2.0"),sQuery(id+"F19.wireOp",EDGE,"E22.2.3.0"),sQuery(id+"F19.wireOp",EDGE,"E22.2.4.0"),sQuery(id+"F19.wireOp",EDGE,"E22.2.5.0"),sQuery(id+"F19.wireOp",EDGE,"E22.3.0.0"),sQuery(id+"F19.wireOp",EDGE,"E22.3.1.0"),sQuery(id+"F19.wireOp",EDGE,"E22.3.2.0"),sQuery(id+"F19.wireOp",EDGE,"E22.3.3.0"),sQuery(id+"F19.wireOp",EDGE,"E22.3.4.0"),sQuery(id+"F19.wireOp",EDGE,"E22.3.5.0"),sQuery(id+"F19.wireOp",EDGE,"E22.4.0.0"),sQuery(id+"F19.wireOp",EDGE,"E22.4.1.0"),sQuery(id+"F19.wireOp",EDGE,"E22.4.2.0"),sQuery(id+"F19.wireOp",EDGE,"E22.4.3.0"),sQuery(id+"F19.wireOp",EDGE,"E22.4.4.0"),sQuery(id+"F19.wireOp",EDGE,"E22.4.5.0"),sQuery(id+"F19.wireOp",EDGE,"E22.5.0.0"),sQuery(id+"F19.wireOp",EDGE,"E22.5.1.0"),sQuery(id+"F19.wireOp",EDGE,"E22.5.2.0"),sQuery(id+"F19.wireOp",EDGE,"E22.5.3.0"),sQuery(id+"F19.wireOp",EDGE,"E22.5.4.0"),sQuery(id+"F19.wireOp",EDGE,"E22.5.5.0"),sQuery(id+"F19.wireOp",EDGE,"E22.6.0.0"),sQuery(id+"F19.wireOp",EDGE,"E22.6.1.0"),sQuery(id+"F19.wireOp",EDGE,"E22.6.2.0"),sQuery(id+"F19.wireOp",EDGE,"E22.6.3.0"),sQuery(id+"F19.wireOp",EDGE,"E22.6.4.0"),sQuery(id+"F19.wireOp",EDGE,"E22.6.5.0"),sQuery(id+"F19.wireOp",EDGE,"E22.7.0.0"),sQuery(id+"F19.wireOp",EDGE,"E22.7.1.0"),sQuery(id+"F19.wireOp",EDGE,"E22.7.2.0"),sQuery(id+"F19.wireOp",EDGE,"E22.7.3.0"),sQuery(id+"F19.wireOp",EDGE,"E22.7.4.0"),sQuery(id+"F19.wireOp",EDGE,"E22.7.5.0"),sQuery(id+"F19.wireOp",EDGE,"E22.8.0.0"),sQuery(id+"F19.wireOp",EDGE,"E22.8.1.0"),sQuery(id+"F19.wireOp",EDGE,"E22.8.2.0"),sQuery(id+"F19.wireOp",EDGE,"E22.8.3.0"),sQuery(id+"F19.wireOp",EDGE,"E22.8.4.0"),sQuery(id+"F19.wireOp",EDGE,"E22.8.5.0"),sQuery(id+"F19.wireOp",EDGE,"E22.9.0.0"),sQuery(id+"F19.wireOp",EDGE,"E22.9.1.0"),sQuery(id+"F19.wireOp",EDGE,"E22.9.2.0"),sQuery(id+"F19.wireOp",EDGE,"E22.9.3.0"),sQuery(id+"F19.wireOp",EDGE,"E22.9.4.0"),sQuery(id+"F19.wireOp",EDGE,"E22.9.5.0"),sQuery(id+"F19.wireOp",EDGE,"E22.10.0.0"),sQuery(id+"F19.wireOp",EDGE,"E22.10.1.0"),sQuery(id+"F19.wireOp",EDGE,"E22.10.2.0"),sQuery(id+"F19.wireOp",EDGE,"E22.10.3.0"),sQuery(id+"F19.wireOp",EDGE,"E22.10.4.0"),sQuery(id+"F19.wireOp",EDGE,"E22.10.5.0"),sQuery(id+"F19.wireOp",EDGE,"E22.11.0.0"),sQuery(id+"F19.wireOp",EDGE,"E22.11.1.0"),sQuery(id+"F19.wireOp",EDGE,"E22.11.2.0"),sQuery(id+"F19.wireOp",EDGE,"E22.11.3.0"),sQuery(id+"F19.wireOp",EDGE,"E22.11.4.0"),sQuery(id+"F19.wireOp",EDGE,"E22.11.5.0"),sQuery(id+"F19.wireOp",EDGE,"E22.12.0.0"),sQuery(id+"F19.wireOp",EDGE,"E22.12.1.0"),sQuery(id+"F19.wireOp",EDGE,"E22.12.2.0"),sQuery(id+"F19.wireOp",EDGE,"E22.12.3.0"),sQuery(id+"F19.wireOp",EDGE,"E22.12.4.0"),sQuery(id+"F19.wireOp",EDGE,"E22.12.5.0")])]});
            var Q8;
            Q8=makeQuery(id+"F22.opExtrude","SWEPT_BODY",BODY,{"disambiguationData":[OSD([sQuery(id+"F21.wireOp",EDGE,"E23.0.0"),sQuery(id+"F21.wireOp",EDGE,"E23.0.1"),sQuery(id+"F21.wireOp",EDGE,"E23.0.2"),sQuery(id+"F21.wireOp",EDGE,"E23.0.3"),sQuery(id+"F21.wireOp",EDGE,"E24.0"),sQuery(id+"F21.wireOp",EDGE,"E25.0.1.0"),sQuery(id+"F21.wireOp",EDGE,"E25.0.2.0"),sQuery(id+"F21.wireOp",EDGE,"E25.0.3.0"),sQuery(id+"F21.wireOp",EDGE,"E25.0.4.0"),sQuery(id+"F21.wireOp",EDGE,"E25.0.5.0"),sQuery(id+"F21.wireOp",EDGE,"E25.1.0.0"),sQuery(id+"F21.wireOp",EDGE,"E25.1.1.0"),sQuery(id+"F21.wireOp",EDGE,"E25.1.2.0"),sQuery(id+"F21.wireOp",EDGE,"E25.1.3.0"),sQuery(id+"F21.wireOp",EDGE,"E25.1.4.0"),sQuery(id+"F21.wireOp",EDGE,"E25.1.5.0"),sQuery(id+"F21.wireOp",EDGE,"E25.2.0.0"),sQuery(id+"F21.wireOp",EDGE,"E25.2.1.0"),sQuery(id+"F21.wireOp",EDGE,"E25.2.2.0"),sQuery(id+"F21.wireOp",EDGE,"E25.2.3.0"),sQuery(id+"F21.wireOp",EDGE,"E25.2.4.0"),sQuery(id+"F21.wireOp",EDGE,"E25.2.5.0"),sQuery(id+"F21.wireOp",EDGE,"E25.3.0.0"),sQuery(id+"F21.wireOp",EDGE,"E25.3.1.0"),sQuery(id+"F21.wireOp",EDGE,"E25.3.2.0"),sQuery(id+"F21.wireOp",EDGE,"E25.3.3.0"),sQuery(id+"F21.wireOp",EDGE,"E25.3.4.0"),sQuery(id+"F21.wireOp",EDGE,"E25.3.5.0"),sQuery(id+"F21.wireOp",EDGE,"E25.4.0.0"),sQuery(id+"F21.wireOp",EDGE,"E25.4.1.0"),sQuery(id+"F21.wireOp",EDGE,"E25.4.2.0"),sQuery(id+"F21.wireOp",EDGE,"E25.4.3.0"),sQuery(id+"F21.wireOp",EDGE,"E25.4.4.0"),sQuery(id+"F21.wireOp",EDGE,"E25.4.5.0"),sQuery(id+"F21.wireOp",EDGE,"E25.5.0.0"),sQuery(id+"F21.wireOp",EDGE,"E25.5.1.0"),sQuery(id+"F21.wireOp",EDGE,"E25.5.2.0"),sQuery(id+"F21.wireOp",EDGE,"E25.5.3.0"),sQuery(id+"F21.wireOp",EDGE,"E25.5.4.0"),sQuery(id+"F21.wireOp",EDGE,"E25.5.5.0"),sQuery(id+"F21.wireOp",EDGE,"E25.6.0.0"),sQuery(id+"F21.wireOp",EDGE,"E25.6.1.0"),sQuery(id+"F21.wireOp",EDGE,"E25.6.2.0"),sQuery(id+"F21.wireOp",EDGE,"E25.6.3.0"),sQuery(id+"F21.wireOp",EDGE,"E25.6.4.0"),sQuery(id+"F21.wireOp",EDGE,"E25.6.5.0"),sQuery(id+"F21.wireOp",EDGE,"E25.7.0.0"),sQuery(id+"F21.wireOp",EDGE,"E25.7.1.0"),sQuery(id+"F21.wireOp",EDGE,"E25.7.2.0"),sQuery(id+"F21.wireOp",EDGE,"E25.7.3.0"),sQuery(id+"F21.wireOp",EDGE,"E25.7.4.0"),sQuery(id+"F21.wireOp",EDGE,"E25.7.5.0"),sQuery(id+"F21.wireOp",EDGE,"E25.8.0.0"),sQuery(id+"F21.wireOp",EDGE,"E25.8.1.0"),sQuery(id+"F21.wireOp",EDGE,"E25.8.2.0"),sQuery(id+"F21.wireOp",EDGE,"E25.8.3.0"),sQuery(id+"F21.wireOp",EDGE,"E25.8.4.0"),sQuery(id+"F21.wireOp",EDGE,"E25.8.5.0"),sQuery(id+"F21.wireOp",EDGE,"E25.9.0.0"),sQuery(id+"F21.wireOp",EDGE,"E25.9.1.0"),sQuery(id+"F21.wireOp",EDGE,"E25.9.2.0"),sQuery(id+"F21.wireOp",EDGE,"E25.9.3.0"),sQuery(id+"F21.wireOp",EDGE,"E25.9.4.0"),sQuery(id+"F21.wireOp",EDGE,"E25.9.5.0"),sQuery(id+"F21.wireOp",EDGE,"E25.10.0.0"),sQuery(id+"F21.wireOp",EDGE,"E25.10.1.0"),sQuery(id+"F21.wireOp",EDGE,"E25.10.2.0"),sQuery(id+"F21.wireOp",EDGE,"E25.10.3.0"),sQuery(id+"F21.wireOp",EDGE,"E25.10.4.0"),sQuery(id+"F21.wireOp",EDGE,"E25.10.5.0"),sQuery(id+"F21.wireOp",EDGE,"E25.11.0.0"),sQuery(id+"F21.wireOp",EDGE,"E25.11.1.0"),sQuery(id+"F21.wireOp",EDGE,"E25.11.2.0"),sQuery(id+"F21.wireOp",EDGE,"E25.11.3.0"),sQuery(id+"F21.wireOp",EDGE,"E25.11.4.0"),sQuery(id+"F21.wireOp",EDGE,"E25.11.5.0"),sQuery(id+"F21.wireOp",EDGE,"E25.12.0.0"),sQuery(id+"F21.wireOp",EDGE,"E25.12.1.0"),sQuery(id+"F21.wireOp",EDGE,"E25.12.2.0"),sQuery(id+"F21.wireOp",EDGE,"E25.12.3.0"),sQuery(id+"F21.wireOp",EDGE,"E25.12.4.0"),sQuery(id+"F21.wireOp",EDGE,"E25.12.5.0")])]});
            var Q9;
            Q9=makeQuery(id+"F23.opPattern","COPY",BODY,{"derivedFrom":makeQuery(id+"F20.opExtrude","SWEPT_BODY",BODY,{"disambiguationData":[OSD([sQuery(id+"F19.wireOp",EDGE,"E20.bottom"),sQuery(id+"F19.wireOp",EDGE,"E20.top"),sQuery(id+"F19.wireOp",EDGE,"E20.left"),sQuery(id+"F19.wireOp",EDGE,"E20.right"),sQuery(id+"F19.wireOp",EDGE,"E21"),sQuery(id+"F19.wireOp",EDGE,"E22.0.1.0"),sQuery(id+"F19.wireOp",EDGE,"E22.0.2.0"),sQuery(id+"F19.wireOp",EDGE,"E22.0.3.0"),sQuery(id+"F19.wireOp",EDGE,"E22.0.4.0"),sQuery(id+"F19.wireOp",EDGE,"E22.0.5.0"),sQuery(id+"F19.wireOp",EDGE,"E22.1.0.0"),sQuery(id+"F19.wireOp",EDGE,"E22.1.1.0"),sQuery(id+"F19.wireOp",EDGE,"E22.1.2.0"),sQuery(id+"F19.wireOp",EDGE,"E22.1.3.0"),sQuery(id+"F19.wireOp",EDGE,"E22.1.4.0"),sQuery(id+"F19.wireOp",EDGE,"E22.1.5.0"),sQuery(id+"F19.wireOp",EDGE,"E22.2.0.0"),sQuery(id+"F19.wireOp",EDGE,"E22.2.1.0"),sQuery(id+"F19.wireOp",EDGE,"E22.2.2.0"),sQuery(id+"F19.wireOp",EDGE,"E22.2.3.0"),sQuery(id+"F19.wireOp",EDGE,"E22.2.4.0"),sQuery(id+"F19.wireOp",EDGE,"E22.2.5.0"),sQuery(id+"F19.wireOp",EDGE,"E22.3.0.0"),sQuery(id+"F19.wireOp",EDGE,"E22.3.1.0"),sQuery(id+"F19.wireOp",EDGE,"E22.3.2.0"),sQuery(id+"F19.wireOp",EDGE,"E22.3.3.0"),sQuery(id+"F19.wireOp",EDGE,"E22.3.4.0"),sQuery(id+"F19.wireOp",EDGE,"E22.3.5.0"),sQuery(id+"F19.wireOp",EDGE,"E22.4.0.0"),sQuery(id+"F19.wireOp",EDGE,"E22.4.1.0"),sQuery(id+"F19.wireOp",EDGE,"E22.4.2.0"),sQuery(id+"F19.wireOp",EDGE,"E22.4.3.0"),sQuery(id+"F19.wireOp",EDGE,"E22.4.4.0"),sQuery(id+"F19.wireOp",EDGE,"E22.4.5.0"),sQuery(id+"F19.wireOp",EDGE,"E22.5.0.0"),sQuery(id+"F19.wireOp",EDGE,"E22.5.1.0"),sQuery(id+"F19.wireOp",EDGE,"E22.5.2.0"),sQuery(id+"F19.wireOp",EDGE,"E22.5.3.0"),sQuery(id+"F19.wireOp",EDGE,"E22.5.4.0"),sQuery(id+"F19.wireOp",EDGE,"E22.5.5.0"),sQuery(id+"F19.wireOp",EDGE,"E22.6.0.0"),sQuery(id+"F19.wireOp",EDGE,"E22.6.1.0"),sQuery(id+"F19.wireOp",EDGE,"E22.6.2.0"),sQuery(id+"F19.wireOp",EDGE,"E22.6.3.0"),sQuery(id+"F19.wireOp",EDGE,"E22.6.4.0"),sQuery(id+"F19.wireOp",EDGE,"E22.6.5.0"),sQuery(id+"F19.wireOp",EDGE,"E22.7.0.0"),sQuery(id+"F19.wireOp",EDGE,"E22.7.1.0"),sQuery(id+"F19.wireOp",EDGE,"E22.7.2.0"),sQuery(id+"F19.wireOp",EDGE,"E22.7.3.0"),sQuery(id+"F19.wireOp",EDGE,"E22.7.4.0"),sQuery(id+"F19.wireOp",EDGE,"E22.7.5.0"),sQuery(id+"F19.wireOp",EDGE,"E22.8.0.0"),sQuery(id+"F19.wireOp",EDGE,"E22.8.1.0"),sQuery(id+"F19.wireOp",EDGE,"E22.8.2.0"),sQuery(id+"F19.wireOp",EDGE,"E22.8.3.0"),sQuery(id+"F19.wireOp",EDGE,"E22.8.4.0"),sQuery(id+"F19.wireOp",EDGE,"E22.8.5.0"),sQuery(id+"F19.wireOp",EDGE,"E22.9.0.0"),sQuery(id+"F19.wireOp",EDGE,"E22.9.1.0"),sQuery(id+"F19.wireOp",EDGE,"E22.9.2.0"),sQuery(id+"F19.wireOp",EDGE,"E22.9.3.0"),sQuery(id+"F19.wireOp",EDGE,"E22.9.4.0"),sQuery(id+"F19.wireOp",EDGE,"E22.9.5.0"),sQuery(id+"F19.wireOp",EDGE,"E22.10.0.0"),sQuery(id+"F19.wireOp",EDGE,"E22.10.1.0"),sQuery(id+"F19.wireOp",EDGE,"E22.10.2.0"),sQuery(id+"F19.wireOp",EDGE,"E22.10.3.0"),sQuery(id+"F19.wireOp",EDGE,"E22.10.4.0"),sQuery(id+"F19.wireOp",EDGE,"E22.10.5.0"),sQuery(id+"F19.wireOp",EDGE,"E22.11.0.0"),sQuery(id+"F19.wireOp",EDGE,"E22.11.1.0"),sQuery(id+"F19.wireOp",EDGE,"E22.11.2.0"),sQuery(id+"F19.wireOp",EDGE,"E22.11.3.0"),sQuery(id+"F19.wireOp",EDGE,"E22.11.4.0"),sQuery(id+"F19.wireOp",EDGE,"E22.11.5.0"),sQuery(id+"F19.wireOp",EDGE,"E22.12.0.0"),sQuery(id+"F19.wireOp",EDGE,"E22.12.1.0"),sQuery(id+"F19.wireOp",EDGE,"E22.12.2.0"),sQuery(id+"F19.wireOp",EDGE,"E22.12.3.0"),sQuery(id+"F19.wireOp",EDGE,"E22.12.4.0"),sQuery(id+"F19.wireOp",EDGE,"E22.12.5.0")])]}),"instanceName":"1"});
            var Q10;
            Q10=makeQuery(id+"F25.opExtrude","SWEPT_BODY",BODY,{"disambiguationData":[OSD([sQuery(id+"F24.wireOp",EDGE,"E26.0"),sQuery(id+"F24.wireOp",EDGE,"E27.0"),sQuery(id+"F24.wireOp",EDGE,"E27.1"),sQuery(id+"F24.wireOp",EDGE,"E27.2"),sQuery(id+"F24.wireOp",EDGE,"E27.3"),sQuery(id+"F24.wireOp",EDGE,"E27.4"),sQuery(id+"F24.wireOp",EDGE,"E27.5")])]});
            var Q11;
            Q11=makeQuery(id+"F25.opExtrude","SWEPT_BODY",BODY,{"disambiguationData":[OSD([sQuery(id+"F24.wireOp",EDGE,"E28.0"),sQuery(id+"F24.wireOp",EDGE,"E31.0"),sQuery(id+"F24.wireOp",EDGE,"E31.1"),sQuery(id+"F24.wireOp",EDGE,"E31.2"),sQuery(id+"F24.wireOp",EDGE,"E31.3"),sQuery(id+"F24.wireOp",EDGE,"E31.4"),sQuery(id+"F24.wireOp",EDGE,"E31.5")])]});
            var Q12;
            Q12=makeQuery(id+"F23.opPattern","COPY",BODY,{"derivedFrom":makeQuery(id+"F22.opExtrude","SWEPT_BODY",BODY,{"disambiguationData":[OSD([sQuery(id+"F21.wireOp",EDGE,"E23.0.0"),sQuery(id+"F21.wireOp",EDGE,"E23.0.1"),sQuery(id+"F21.wireOp",EDGE,"E23.0.2"),sQuery(id+"F21.wireOp",EDGE,"E23.0.3"),sQuery(id+"F21.wireOp",EDGE,"E24.0"),sQuery(id+"F21.wireOp",EDGE,"E25.0.1.0"),sQuery(id+"F21.wireOp",EDGE,"E25.0.2.0"),sQuery(id+"F21.wireOp",EDGE,"E25.0.3.0"),sQuery(id+"F21.wireOp",EDGE,"E25.0.4.0"),sQuery(id+"F21.wireOp",EDGE,"E25.0.5.0"),sQuery(id+"F21.wireOp",EDGE,"E25.1.0.0"),sQuery(id+"F21.wireOp",EDGE,"E25.1.1.0"),sQuery(id+"F21.wireOp",EDGE,"E25.1.2.0"),sQuery(id+"F21.wireOp",EDGE,"E25.1.3.0"),sQuery(id+"F21.wireOp",EDGE,"E25.1.4.0"),sQuery(id+"F21.wireOp",EDGE,"E25.1.5.0"),sQuery(id+"F21.wireOp",EDGE,"E25.2.0.0"),sQuery(id+"F21.wireOp",EDGE,"E25.2.1.0"),sQuery(id+"F21.wireOp",EDGE,"E25.2.2.0"),sQuery(id+"F21.wireOp",EDGE,"E25.2.3.0"),sQuery(id+"F21.wireOp",EDGE,"E25.2.4.0"),sQuery(id+"F21.wireOp",EDGE,"E25.2.5.0"),sQuery(id+"F21.wireOp",EDGE,"E25.3.0.0"),sQuery(id+"F21.wireOp",EDGE,"E25.3.1.0"),sQuery(id+"F21.wireOp",EDGE,"E25.3.2.0"),sQuery(id+"F21.wireOp",EDGE,"E25.3.3.0"),sQuery(id+"F21.wireOp",EDGE,"E25.3.4.0"),sQuery(id+"F21.wireOp",EDGE,"E25.3.5.0"),sQuery(id+"F21.wireOp",EDGE,"E25.4.0.0"),sQuery(id+"F21.wireOp",EDGE,"E25.4.1.0"),sQuery(id+"F21.wireOp",EDGE,"E25.4.2.0"),sQuery(id+"F21.wireOp",EDGE,"E25.4.3.0"),sQuery(id+"F21.wireOp",EDGE,"E25.4.4.0"),sQuery(id+"F21.wireOp",EDGE,"E25.4.5.0"),sQuery(id+"F21.wireOp",EDGE,"E25.5.0.0"),sQuery(id+"F21.wireOp",EDGE,"E25.5.1.0"),sQuery(id+"F21.wireOp",EDGE,"E25.5.2.0"),sQuery(id+"F21.wireOp",EDGE,"E25.5.3.0"),sQuery(id+"F21.wireOp",EDGE,"E25.5.4.0"),sQuery(id+"F21.wireOp",EDGE,"E25.5.5.0"),sQuery(id+"F21.wireOp",EDGE,"E25.6.0.0"),sQuery(id+"F21.wireOp",EDGE,"E25.6.1.0"),sQuery(id+"F21.wireOp",EDGE,"E25.6.2.0"),sQuery(id+"F21.wireOp",EDGE,"E25.6.3.0"),sQuery(id+"F21.wireOp",EDGE,"E25.6.4.0"),sQuery(id+"F21.wireOp",EDGE,"E25.6.5.0"),sQuery(id+"F21.wireOp",EDGE,"E25.7.0.0"),sQuery(id+"F21.wireOp",EDGE,"E25.7.1.0"),sQuery(id+"F21.wireOp",EDGE,"E25.7.2.0"),sQuery(id+"F21.wireOp",EDGE,"E25.7.3.0"),sQuery(id+"F21.wireOp",EDGE,"E25.7.4.0"),sQuery(id+"F21.wireOp",EDGE,"E25.7.5.0"),sQuery(id+"F21.wireOp",EDGE,"E25.8.0.0"),sQuery(id+"F21.wireOp",EDGE,"E25.8.1.0"),sQuery(id+"F21.wireOp",EDGE,"E25.8.2.0"),sQuery(id+"F21.wireOp",EDGE,"E25.8.3.0"),sQuery(id+"F21.wireOp",EDGE,"E25.8.4.0"),sQuery(id+"F21.wireOp",EDGE,"E25.8.5.0"),sQuery(id+"F21.wireOp",EDGE,"E25.9.0.0"),sQuery(id+"F21.wireOp",EDGE,"E25.9.1.0"),sQuery(id+"F21.wireOp",EDGE,"E25.9.2.0"),sQuery(id+"F21.wireOp",EDGE,"E25.9.3.0"),sQuery(id+"F21.wireOp",EDGE,"E25.9.4.0"),sQuery(id+"F21.wireOp",EDGE,"E25.9.5.0"),sQuery(id+"F21.wireOp",EDGE,"E25.10.0.0"),sQuery(id+"F21.wireOp",EDGE,"E25.10.1.0"),sQuery(id+"F21.wireOp",EDGE,"E25.10.2.0"),sQuery(id+"F21.wireOp",EDGE,"E25.10.3.0"),sQuery(id+"F21.wireOp",EDGE,"E25.10.4.0"),sQuery(id+"F21.wireOp",EDGE,"E25.10.5.0"),sQuery(id+"F21.wireOp",EDGE,"E25.11.0.0"),sQuery(id+"F21.wireOp",EDGE,"E25.11.1.0"),sQuery(id+"F21.wireOp",EDGE,"E25.11.2.0"),sQuery(id+"F21.wireOp",EDGE,"E25.11.3.0"),sQuery(id+"F21.wireOp",EDGE,"E25.11.4.0"),sQuery(id+"F21.wireOp",EDGE,"E25.11.5.0"),sQuery(id+"F21.wireOp",EDGE,"E25.12.0.0"),sQuery(id+"F21.wireOp",EDGE,"E25.12.1.0"),sQuery(id+"F21.wireOp",EDGE,"E25.12.2.0"),sQuery(id+"F21.wireOp",EDGE,"E25.12.3.0"),sQuery(id+"F21.wireOp",EDGE,"E25.12.4.0"),sQuery(id+"F21.wireOp",EDGE,"E25.12.5.0")])]}),"instanceName":"1"});
            var Q13;
            Q13=makeQuery(id+"F25.opExtrude","SWEPT_BODY",BODY,{"disambiguationData":[OSD([sQuery(id+"F24.wireOp",EDGE,"E30.0"),sQuery(id+"F24.wireOp",EDGE,"E33.0"),sQuery(id+"F24.wireOp",EDGE,"E33.1"),sQuery(id+"F24.wireOp",EDGE,"E33.2"),sQuery(id+"F24.wireOp",EDGE,"E33.3"),sQuery(id+"F24.wireOp",EDGE,"E33.4"),sQuery(id+"F24.wireOp",EDGE,"E33.5")])]});
            var Q14;
            Q14=makeQuery(id+"F25.opExtrude","SWEPT_BODY",BODY,{"disambiguationData":[OSD([sQuery(id+"F24.wireOp",EDGE,"E29.0"),sQuery(id+"F24.wireOp",EDGE,"E32.0"),sQuery(id+"F24.wireOp",EDGE,"E32.1"),sQuery(id+"F24.wireOp",EDGE,"E32.2"),sQuery(id+"F24.wireOp",EDGE,"E32.3"),sQuery(id+"F24.wireOp",EDGE,"E32.4"),sQuery(id+"F24.wireOp",EDGE,"E32.5")])]});
            var Q15;
            Q15=makeQuery(id+"F28.opExtrude","SWEPT_BODY",BODY,{"disambiguationData":[OSD([sQuery(id+"F27.wireOp",EDGE,"E34.bottom"),sQuery(id+"F27.wireOp",EDGE,"E34.top"),sQuery(id+"F27.wireOp",EDGE,"E34.left"),sQuery(id+"F27.wireOp",EDGE,"E34.right")])]});
            var Q16;
            Q16=qCreatedBy(id+"F45.planeOp",FACE);
            mirror(context, id + "F46", {"entities" : qUnion([Q0, Q1, Q2, Q3, Q4, Q5, Q6, Q7, Q8, Q9, Q10, Q11, Q12, Q13, Q14, Q15]), "mirrorPlane" : qUnion([Q16])});
        }
        {
            var Q0;
            {var subQ0=sQuery(id+"F2.wireOp",EDGE,"E1.top");Q0=makeQuery(id+"F46.opPattern","COPY",FACE,{"derivedFrom":makeQuery(id+"F3.boolean.opBoolean","SPLIT",FACE,{"disambiguationData":[TD([makeQuery(id+"F3.opExtrude","SWEPT_FACE",FACE,{"disambiguationData":[OSD([subQ0])]})])],"derivedFrom":makeQuery(id+"F1.opExtrude","SWEPT_FACE",FACE,{"disambiguationData":[OSD([sQuery(id+"F0.wireOp",EDGE,"E0.top")])]})}),"instanceName":"1"});}
            cPlane(context, id + "F47", {"entities" : qUnion([Q0]), "cplaneType" : CPlaneType.OFFSET, "offset" : 635 * mm, "oppositeDirection" : true, "width" : 152.4 * mm, "height" : 152.4 * mm});
        }
        {
            var Q0;
            Q0=qCreatedBy(id+"F47.planeOp",FACE);
            var sketch = newSketch(context, id + "F48", { "sketchPlane" : qUnion([Q0])});
            skLineSegment(sketch, "E54.0", {"start": v(4051.3, 577.85) * mm, "end": v(4051.3, 476.25) * mm});
            skLineSegment(sketch, "E55.0", {"start": v(3111.5, 476.25) * mm, "end": v(3111.5, 577.85) * mm});
            skLineSegment(sketch, "E56", {"start": v(3111.5, 476.25) * mm, "end": v(4051.3, 476.25) * mm});
            skLineSegment(sketch, "E57", {"start": v(4051.3, 577.85) * mm, "end": v(3111.5, 577.85) * mm});
            skLineSegment(sketch, "E58.0", {"start": v(4051.3, -476.25) * mm, "end": v(4051.3, -577.85) * mm});
            skLineSegment(sketch, "E59.0", {"start": v(3111.5, -577.85) * mm, "end": v(3111.5, -476.25) * mm});
            skLineSegment(sketch, "E60", {"start": v(3111.5, -577.85) * mm, "end": v(4051.3, -577.85) * mm});
            skLineSegment(sketch, "E61", {"start": v(3111.5, -476.25) * mm, "end": v(4051.3, -476.25) * mm});
            skSolve(sketch);
        }
        {
            var Q0;
            Q0 = qSketchRegion(id + "F48", true);
            extrude(context, id + "F49", {"entities" : qUnion([Q0]), "oppositeDirection" : true, "depth" : 38.1 * mm, "offsetDistance" : 25.4 * mm});
        }
        {
            var Q0;
            Q0=makeQuery(id+"F46.opPattern","COPY",BODY,{"derivedFrom":makeQuery(id+"F25.opExtrude","SWEPT_BODY",BODY,{"disambiguationData":[OSD([sQuery(id+"F24.wireOp",EDGE,"E26.0"),sQuery(id+"F24.wireOp",EDGE,"E27.0"),sQuery(id+"F24.wireOp",EDGE,"E27.1"),sQuery(id+"F24.wireOp",EDGE,"E27.2"),sQuery(id+"F24.wireOp",EDGE,"E27.3"),sQuery(id+"F24.wireOp",EDGE,"E27.4"),sQuery(id+"F24.wireOp",EDGE,"E27.5")])]}),"instanceName":"1"});
            var Q1;
            Q1=makeQuery(id+"F46.opPattern","COPY",BODY,{"derivedFrom":makeQuery(id+"F25.opExtrude","SWEPT_BODY",BODY,{"disambiguationData":[OSD([sQuery(id+"F24.wireOp",EDGE,"E28.0"),sQuery(id+"F24.wireOp",EDGE,"E31.0"),sQuery(id+"F24.wireOp",EDGE,"E31.1"),sQuery(id+"F24.wireOp",EDGE,"E31.2"),sQuery(id+"F24.wireOp",EDGE,"E31.3"),sQuery(id+"F24.wireOp",EDGE,"E31.4"),sQuery(id+"F24.wireOp",EDGE,"E31.5")])]}),"instanceName":"1"});
            var Q2;
            Q2=makeQuery(id+"F46.opPattern","COPY",BODY,{"derivedFrom":makeQuery(id+"F25.opExtrude","SWEPT_BODY",BODY,{"disambiguationData":[OSD([sQuery(id+"F24.wireOp",EDGE,"E29.0"),sQuery(id+"F24.wireOp",EDGE,"E32.0"),sQuery(id+"F24.wireOp",EDGE,"E32.1"),sQuery(id+"F24.wireOp",EDGE,"E32.2"),sQuery(id+"F24.wireOp",EDGE,"E32.3"),sQuery(id+"F24.wireOp",EDGE,"E32.4"),sQuery(id+"F24.wireOp",EDGE,"E32.5")])]}),"instanceName":"1"});
            var Q3;
            Q3=makeQuery(id+"F46.opPattern","COPY",BODY,{"derivedFrom":makeQuery(id+"F25.opExtrude","SWEPT_BODY",BODY,{"disambiguationData":[OSD([sQuery(id+"F24.wireOp",EDGE,"E30.0"),sQuery(id+"F24.wireOp",EDGE,"E33.0"),sQuery(id+"F24.wireOp",EDGE,"E33.1"),sQuery(id+"F24.wireOp",EDGE,"E33.2"),sQuery(id+"F24.wireOp",EDGE,"E33.3"),sQuery(id+"F24.wireOp",EDGE,"E33.4"),sQuery(id+"F24.wireOp",EDGE,"E33.5")])]}),"instanceName":"1"});
            transform(context, id + "F50", {"entities" : qUnion([Q0, Q1, Q2, Q3]), "transformType" : TransformType.TRANSLATION_3D, "dx" : 0 * mm, "dy" : 0 * mm, "dz" : 673.1 * mm, "makeCopy" : true});
        }
        {
            var Q0;
            Q0=makeQuery(id+"F49.opExtrude","CAP_FACE",FACE,{"disambiguationData":[OSD([sQuery(id+"F48.wireOp",EDGE,"E54.0"),sQuery(id+"F48.wireOp",EDGE,"E55.0"),sQuery(id+"F48.wireOp",EDGE,"E56"),sQuery(id+"F48.wireOp",EDGE,"E57")])],"isStart":false});
            var sketch = newSketch(context, id + "F51", { "sketchPlane" : qUnion([Q0])});
            skLineSegment(sketch, "E62.0.0", {"start": v(3848.1, 679.45) * mm, "end": v(3314.7, 679.45) * mm});
            skLineSegment(sketch, "E62.0.1", {"start": v(3314.7, 679.45) * mm, "end": v(3314.7, -679.45) * mm});
            skLineSegment(sketch, "E62.0.2", {"start": v(3314.7, -679.45) * mm, "end": v(3848.1, -679.45) * mm});
            skLineSegment(sketch, "E62.0.3", {"start": v(3848.1, -679.45) * mm, "end": v(3848.1, 679.45) * mm});
            skSolve(sketch);
        }
        {
            var Q0;
            Q0 = qSketchRegion(id + "F51", true);
            extrude(context, id + "F52", {"entities" : qUnion([Q0]), "depth" : 533.4 * mm, "offsetDistance" : 25.4 * mm});
        }
        {
            var Q0;
            Q0=makeQuery(id+"F49.opExtrude","CAP_EDGE",EDGE,{"disambiguationData":[OSD([sQuery(id+"F48.wireOp",EDGE,"E55.0")])],"isStart":false});
            var Q1;
            Q1=makeQuery(id+"F49.opExtrude","CAP_EDGE",EDGE,{"disambiguationData":[OSD([sQuery(id+"F48.wireOp",EDGE,"E59.0")])],"isStart":false});
            var Q2;
            Q2=makeQuery(id+"F49.opExtrude","CAP_EDGE",EDGE,{"disambiguationData":[OSD([sQuery(id+"F48.wireOp",EDGE,"E54.0")])],"isStart":false});
            var Q3;
            Q3=makeQuery(id+"F49.opExtrude","CAP_EDGE",EDGE,{"disambiguationData":[OSD([sQuery(id+"F48.wireOp",EDGE,"E58.0")])],"isStart":false});
            fillet(context, id + "F53", {"entities" : qUnion([Q0, Q1, Q2, Q3]), "radius" : 12.7 * mm, "tangentPropagation" : true, "allowEdgeOverflow" : false});
        }
    });
